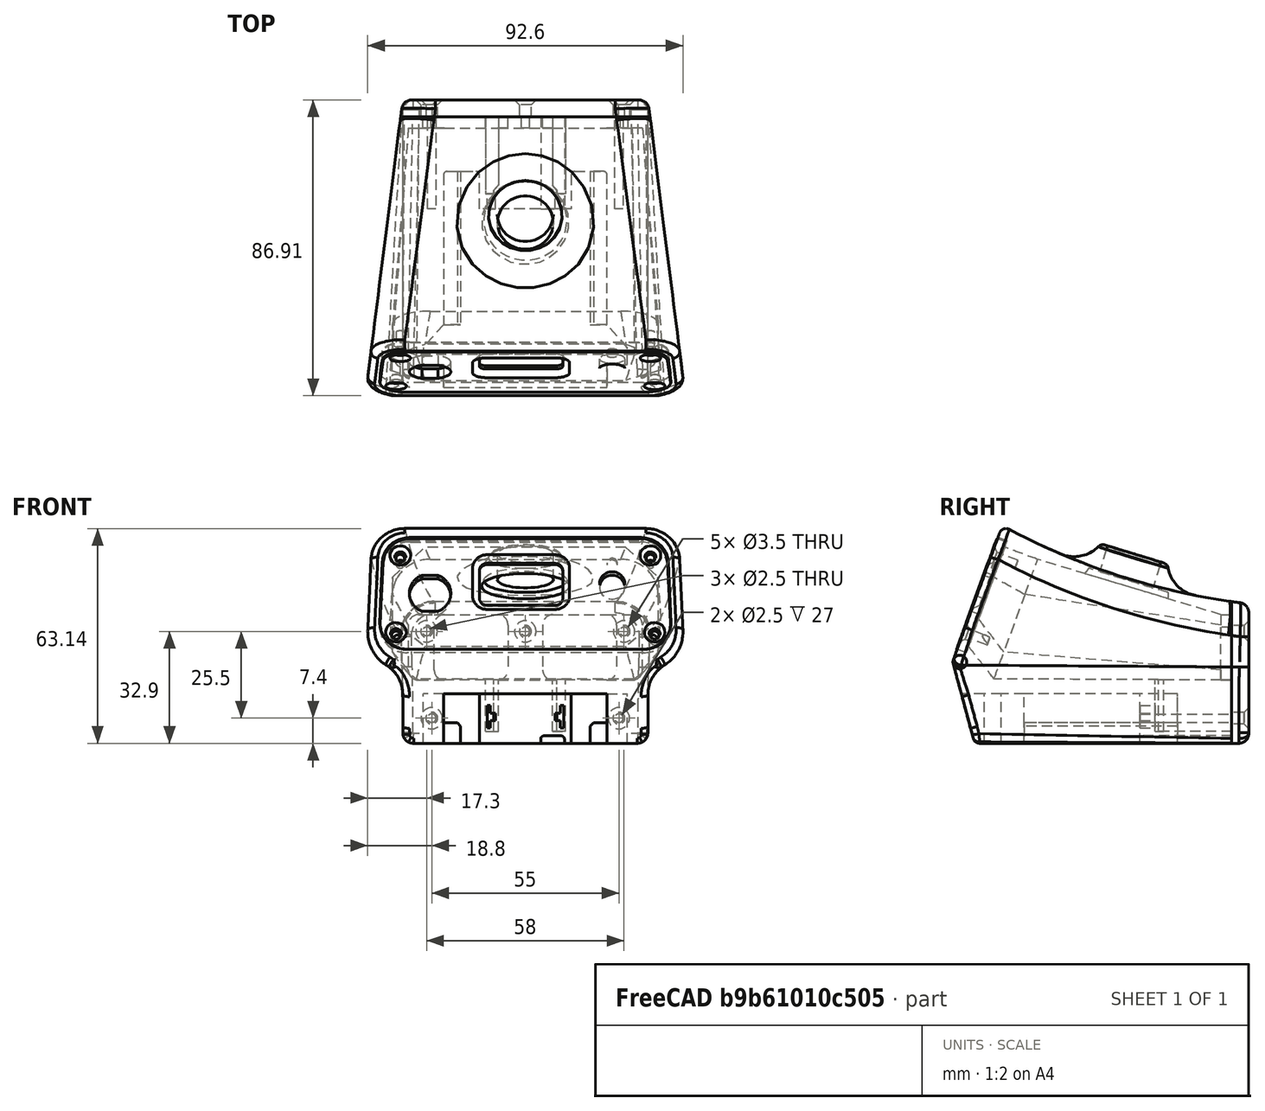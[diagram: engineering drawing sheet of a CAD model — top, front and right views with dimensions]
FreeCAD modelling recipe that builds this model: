
FCSTD DOCUMENT  (FreeCAD 2022.709R28846 (Git))
Label: solder_station4a_snap
License: All rights reserved
LicenseURL: http://en.wikipedia.org/wiki/All_rights_reserved
objects: Sketcher::SketchObject×20, PartDesign::Pocket×10, PartDesign::Fillet×7, Mesh::Feature×4, Part::FeaturePython×3, App::DocumentObjectGroup×3, PartDesign::Chamfer×3, PartDesign::Body×3, PartDesign::FeatureBase×2, PartDesign::Pad×2, Spreadsheet::Sheet×1, Part::Plane×1, Part::Loft×1, Part::Extrusion×1, Part::MultiCommon×1, PartDesign::SubtractiveLoft×1, PartDesign::Revolution×1, PartDesign::Groove×1, App::Part×1
note: 109 computed .brp shape members not serialized (recipe doc carries the construction recipe); baked Part::Feature solids carry a one-line shape summary decoded from their .brp

FEATURE [Sketcher::SketchObject] Sketch  label="RearSupport"
  ArcFitTolerance = 0
  AttachmentOffset = pos=(0,0,-37.8) rot=(0,0,1;0rad)
  AttachmentSupport = -> [XZ_Plane005]
  FullyConstrained = true
  MapMode = 5
  Placement = pos=(0,37.8,8.4e-15) rot=(1,0,0;1.5708rad)
  Support = -> [XZ_Plane005]
  TreeRank = 0
  expr: AttachmentOffset.Base.z = -<<param>>.mid_depth / 2 + <<param>>.wall
  expr: Constraints[24] = 3
  expr: Constraints[37] = <<param>>.bottom_height
  expr: Constraints[38] = <<param>>.floor
  expr: Constraints[39] = <<param>>.rear_height - <<param>>.wall
  expr: Constraints[47] = <<param>>.reart_screw_width2
  expr: Constraints[48] = <<param>>.rear_screw_width1
  expr: Constraints[49] = <<param>>.screw_hole
  expr: Constraints[50] = <<param>>.rear_screw_height
  expr: Constraints[51] = <<param>>.rear_screw_height
  expr: Constraints[52] = <<param>>.rear_screw_offset
  sketch-geometry (22):
    g0: LineSegment StartX=-23.8 StartY=13.8 StartZ=0 EndX=-8.1 EndY=13.8 EndZ=0
    g1: LineSegment StartX=26.8 StartY=10.8 StartZ=0 EndX=26.8 EndY=-2.4 EndZ=0
    g2: LineSegment StartX=23.8 StartY=-5.4 StartZ=0 EndX=8.1 EndY=-5.4 EndZ=0
    g3: LineSegment StartX=-26.8 StartY=-2.4 StartZ=0 EndX=-26.8 EndY=10.8 EndZ=0
    g4: LineSegment StartX=-5.1 StartY=10.8 StartZ=0 EndX=-5.1 EndY=-2.4 EndZ=0
    g5: LineSegment StartX=5.1 StartY=10.8 StartZ=0 EndX=5.1 EndY=-2.4 EndZ=0
    g6: LineSegment StartX=8.1 StartY=13.8 StartZ=0 EndX=23.8 EndY=13.8 EndZ=0
    g7: LineSegment StartX=-8.1 StartY=-5.4 StartZ=0 EndX=-23.8 EndY=-5.4 EndZ=0
    g8: ArcOfCircle CenterX=-8.1 CenterY=10.8 CenterZ=0 NormalX=0 NormalY=0 NormalZ=1 AngleXU=0 Radius=3 StartAngle=0 EndAngle=1.5708
    g9: ArcOfCircle CenterX=8.1 CenterY=10.8 CenterZ=0 NormalX=0 NormalY=0 NormalZ=1 AngleXU=0 Radius=3 StartAngle=1.5708 EndAngle=3.14159
    g10: ArcOfCircle CenterX=-8.1 CenterY=-2.4 CenterZ=0 NormalX=0 NormalY=0 NormalZ=1 AngleXU=0 Radius=3 StartAngle=4.71239 EndAngle=6.28319
    g11: ArcOfCircle CenterX=8.1 CenterY=-2.4 CenterZ=0 NormalX=0 NormalY=0 NormalZ=1 AngleXU=0 Radius=3 StartAngle=3.14159 EndAngle=4.71239
    g12: ArcOfCircle CenterX=-23.8 CenterY=10.8 CenterZ=0 NormalX=0 NormalY=0 NormalZ=1 AngleXU=0 Radius=3 StartAngle=1.5708 EndAngle=3.14159
    g13: ArcOfCircle CenterX=-23.8 CenterY=-2.4 CenterZ=0 NormalX=0 NormalY=0 NormalZ=1 AngleXU=0 Radius=3 StartAngle=3.14159 EndAngle=4.71239
    g14: ArcOfCircle CenterX=23.8 CenterY=10.8 CenterZ=0 NormalX=0 NormalY=0 NormalZ=1 AngleXU=0 Radius=3 StartAngle=0 EndAngle=1.5708
    g15: ArcOfCircle CenterX=23.8 CenterY=-2.4 CenterZ=0 NormalX=0 NormalY=0 NormalZ=1 AngleXU=0 Radius=3 StartAngle=4.71239 EndAngle=6.28319
    g16: Circle [constr] CenterX=0 CenterY=-24 CenterZ=0 NormalX=0 NormalY=0 NormalZ=1 AngleXU=0 Radius=3
    g17: Circle CenterX=0 CenterY=8.9 CenterZ=0 NormalX=0 NormalY=0 NormalZ=1 AngleXU=0 Radius=1.25
    g18: Circle CenterX=-29 CenterY=8.9 CenterZ=0 NormalX=0 NormalY=0 NormalZ=1 AngleXU=0 Radius=1.25
    g19: Circle [constr] CenterX=-27.5 CenterY=-16.6 CenterZ=0 NormalX=0 NormalY=0 NormalZ=1 AngleXU=0 Radius=1.25
    g20: Circle [constr] CenterX=27.5 CenterY=-16.6 CenterZ=0 NormalX=0 NormalY=0 NormalZ=1 AngleXU=0 Radius=1.25
    g21: Circle CenterX=29 CenterY=8.9 CenterZ=0 NormalX=0 NormalY=0 NormalZ=1 AngleXU=0 Radius=1.25
  constraints (53):
    c: Horizontal(g0)
    c: Horizontal(g2)
    c: Vertical(g1)
    c: Vertical(g3)
    c: Vertical(g4)
    c: Vertical(g5)
    c: Tangent(g0,g6)
    c: Tangent(g2,g7)
    c: Tangent(g0,g8) = 1.5708
    c: Tangent(g4,g8) = 1.5708
    c: Tangent(g5,g9) = -1.5708
    c: Tangent(g6,g9) = 1.5708
    c: Tangent(g7,g10) = 1.5708
    c: Tangent(g4,g10) = 1.5708
    c: Tangent(g5,g11) = -1.5708
    c: Tangent(g2,g11) = 1.5708
    c: Tangent(g0,g12) = 1.5708
    c: Tangent(g3,g12) = 1.5708
    c: Tangent(g3,g13) = 1.5708
    c: Tangent(g7,g13) = 1.5708
    c: Tangent(g6,g14) = 1.5708
    c: Tangent(g1,g14) = 1.5708
    c: Tangent(g1,g15) = 1.5708
    c: Tangent(g2,g15) = 1.5708
    c: Radius(g9) = 3
    c: Equal(g12,g13)
    c: Equal(g13,g10)
    c: Equal(g10,g8)
    c: Equal(g11,g15)
    c: Equal(g15,g14)
    c: Equal(g14,g9)
    c: DistanceX(g4,g-1) = 5.1
    c: DistanceX(g5,g1) = 21.7
    c: Symmetric(g4,g5,g-2)
    c: Equal(g7,g2)
    c: PointOnObject(g16,g-2)
    c: Radius(g16) = 3
    c: DistanceY(g16,g-1) = 24
    c: DistanceY(g16,g2) = 18.6
    c: DistanceY(g16,g6) = 37.8
    c: PointOnObject(g17,g-2)
    c: Equal(g21,g18)
    c: Equal(g18,g19)
    c: Equal(g19,g20)
    c: Equal(g18,g17)
    c: Symmetric(g20,g19,g-2)
    c: Symmetric(g18,g21,g-2)
    c: DistanceX(g19,g20) = 55
    c: DistanceX(g18,g21) = 58
    c: Diameter(g19) = 2.5
    c: DistanceY(g20,g21) = 25.5
    c: DistanceY(g20,g17) = 25.5
    c: DistanceY(g16,g19) = 7.4
FEATURE [Spreadsheet::Sheet] Spreadsheet  label="param"
  PythonMode = false
  ShowCells = 0
  TreeRank = 0
  cells = A1=Body; B2=top_depth; C2(top_depth)=70; B3=mid_depth; C3(mid_depth)=82; D3=Half value is the rear reference point; B4=bottom_depth; C4(bottom_depth)=75; B6=bottom_width; C6(bottom_width)=72; B7=bottom_height; C7(bottom_height)=24; B8=bottom_angle; C8(bottom_angle)=15; B10=rear_width; C10(rear_width)=72; B11=rear_height; C11(rear_height)=41; B13=mid_width; C13(mid_width)=80; B14=mid_height; C14(mid_height)=50; B16=front_width1; C16(front_width1)=91; D16=@top (upper); B17=front_width2; C17(front_width2)=94; D17=@mid (lower); B18=front_height; C18(front_height)=64; B19=front_angle; C19(front_angle)=20; D19=20 is actual value; B21=wall; C21(wall)=3.2; B22=radius_big; C22(radius_big)=10; B23=radius_small; C23(radius_small)=3; B24=arch; C24(arch)=200; A26=Button; B27=button_offset; C27(button_offset)=10; B28=button_inside_dia; C28(button_inside_dia)=20; B29=button_outside_dia; C29(button_outside_dia)=22; B30=button_height; C30(button_height)=24; B31=button_extension; C31(button_extension)=8; B32=button_fillet; C32(button_fillet)=12; B33=button_angle; C33(button_angle)=-17; B34=button_hole; C34(button_hole)=16.4; B35=button_hole_center; C35(button_hole_center)=-0.5; A37=Battery Cuts; B38=batt_carveout; C38(batt_carveout)=14.6; B39=batt_rail; C39(batt_rail)=6; B40=batt_rail_length; C40(batt_rail_length)=45; A42=Terminal Pockets; B43=terminal_height; C43(terminal_height)=6.6; B44=terminal_thickness; C44(terminal_thickness)=1; B45=terminal_seperation; C45(terminal_seperation)=21.5; B46=terminal_offset; C46(terminal_offset)=4.5; B47=terminal_depth; C47(terminal_depth)=22.5; A49=Box Interior; B50=floor; C50(floor)=18.6; B51=rear_inside_width; C51(rear_inside_width)==C10 - C21; D51=Calculated; B52=rear_inside_height; C52(rear_inside_height)==C11 - C21; D52=Calculated; B53=mid_inside_width; C53(mid_inside_width)==C13; D53=Calculated; B54=mid_inside_height; C54(mid_inside_height)==C14 + 6; D54=Calculated; B55=front_inside_width1; C55(front_inside_width1)==C62 - C58 * 2; D55=Calculated (upper); B56=front_inside_width2; C56(front_inside_width2)==C63 - C58 * 2; D56=Calculated (lower); B57=front_inside_height; C57(front_inside_height)==C64 - C59 * 2; D57=Calculated; B58=front_width_lip_width; C58(front_width_lip_width)=3; B59=front_inside_lip_height; C59(front_inside_lip_height)=2; A61=Face; B62=face_width1; C62(face_width1)=84; D62=Dimension of opening in case (upper); B63=face_width2; C63(face_width2)=85.5; D63=Dimension of opening in case (lower); B64=face_height; C64(face_height)==34 + 1; D64=Dimension of actual opening in case; B65=face_fit; C65(face_fit)=0.4; D65=Reduction of face dimensions for clearance with case; B66=face_thickness; C66(face_thickness)=3; D66=Face thickness; B67=face_radius; C67(face_radius)=8; D67=Corner radius; B68=face_offset; C68(face_offset)=2.8; D68=Axis origin to bottom face (reference); B69=face_knob_x; C69(face_knob_x)=25.5; D69=Vertical center line of face to center of knob; B70=face_knob_y; C70(face_knob_y)=20.5; D70=Bottom of face to center of knob; B71=face_knob_tab; C71(face_knob_tab)=7; D71=Center to center distance of rotary dial shaft to tab; B72=face_knob_hole; C72(face_knob_hole)=7.4; D72=Hole size fo shaft; B73=face_screen_x; C73(face_screen_x)=14.5; D73=Center of knob to right edge of screen; B74=face_screen_y; C74(face_screen_y)=21; D74=Bottom of face to center of screen; B75=face_screen_width; C75(face_screen_width)=24.5; D75=Width of screen opening; B76=face_screen_height; C76(face_screen_height)=13.1; D76=Height of screen opening; B77=face_screen_radius; C77(face_screen_radius)=2.25; D77=Radius of screen opening; B78=face_plug_x; C78(face_plug_x)=28; D78=Center line of face to center of plug; B79=face_plug_y; C79(face_plug_y)=17.5; D79=Bottom of face to center of plug; B80=face_plug_hole; C80(face_plug_hole)=12.2; D80=Hole size for plug body; A82=Screws; B83=screw_hole; C83(screw_hole)=2.5; D83=Screw hole diameter; B85=front_screw_width1; C85(front_screw_width1)=73.5; D85=Screw center to center distance (upper); B86=front_screw_width2; C86(front_screw_width2)=76; D86=Screw center to center distance (lower); B87=front_screw_height; C87(front_screw_height)=24; D87=Screw center to center distance (top to bottom); B88=front_screw_offset; C88(front_screw_offset)=5.5; D88=Bottom of face to center of screws (lower); B90=rear_screw_width1; C90(rear_screw_width1)=58; D90=Screw center to center distance (upper); B91=reart_screw_width2; C91(reart_screw_width2)=55; D91=Screw center to center distance (lower); B92=rear_screw_height; C92(rear_screw_height)=25.5; D92=Screw center to center distance (top to bottom); B93=rear_screw_offset; C93(rear_screw_offset)=7.4; A95=Back; B96=back_thickness; C96(back_thickness)=5
FEATURE [Sketcher::SketchObject] Sketch008  label="SketchButtonHole"
  ArcFitTolerance = 0
  AttachmentOffset = pos=(0,-0.5,24) rot=(1,0,0;-0.296706rad)
  AttachmentSupport = -> [XY_Plane005]
  FullyConstrained = true
  MapMode = 5
  Placement = pos=(0,-0.5,24) rot=(1,0,0;5.98648rad)
  Support = -> [XY_Plane005]
  TreeRank = 0
  expr: AttachmentOffset.Base.y = <<param>>.button_hole_center
  expr: AttachmentOffset.Base.z = <<param>>.button_height
  expr: AttachmentOffset.Rotation.Angle = <<param>>.button_angle
  expr: Constraints[0] = <<param>>.button_hole
  expr: Constraints[2] = <<param>>.button_offset
  sketch-geometry (1):
    g0: Circle CenterX=0 CenterY=10 CenterZ=0 NormalX=0 NormalY=0 NormalZ=1 AngleXU=0 Radius=8.2
  constraints (3):
    c: Diameter(g0) = 16.4
    c: PointOnObject(g0,g-2)
    c: DistanceY(g-1,g0) = 10
FEATURE [Sketcher::SketchObject] Sketch012  label="SketchSide"
  ArcFitTolerance = 0
  AttachmentOffset = pos=(2.5,0,0) rot=(0,0,1;0rad)
  AttachmentSupport = -> [YZ_Plane006]
  FullyConstrained = true
  MapMode = 5
  Placement = pos=(6e-16,2.5,-6e-16) rot=(0.57735,0.57735,0.57735;2.0944rad)
  Support = -> [YZ_Plane006]
  TreeRank = 0
  expr: AttachmentOffset.Base.x = <<param>>.back_thickness / 2
  expr: Constraints[10] = <<param>>.bottom_height
  expr: Constraints[11] = 90 - <<param>>.bottom_angle
  expr: Constraints[12] = 90 - <<param>>.front_angle
  expr: Constraints[16] = <<param>>.front_height
  expr: Constraints[4] = <<param>>.rear_height - <<param>>.bottom_height
  expr: Constraints[5] = <<param>>.arch
  expr: Constraints[6] = <<param>>.mid_depth + <<param>>.back_thickness
  sketch-geometry (6):
    g0: LineSegment StartX=43.5 StartY=0 StartZ=0 EndX=43.5 EndY=17 EndZ=0
    g1: LineSegment StartX=-43.5 StartY=0 StartZ=0 EndX=-28.9412 EndY=40 EndZ=0
    g2: ArcOfCircle CenterX=66.6993 CenterY=215.65 CenterZ=0 NormalX=0 NormalY=0 NormalZ=1 AngleXU=0 Radius=200 StartAngle=4.21378 EndAngle=4.59613
    g3: LineSegment StartX=-43.5 StartY=0 StartZ=0 EndX=-37.0692 EndY=-24 EndZ=0
    g4: LineSegment StartX=-37.0692 StartY=-24 StartZ=0 EndX=43.5 EndY=-24 EndZ=0
    g5: LineSegment StartX=43.5 StartY=-24 StartZ=0 EndX=43.5 EndY=0 EndZ=0
  constraints (18):
    c: PointOnObject(g1,g-1)
    c: Vertical(g0)
    c: Coincident(g2,g0)
    c: Symmetric(g1,g0,g-2)
    c: DistanceY(g0,g0) = 17
    c: Radius(g2) = 200
    c: DistanceX(g1,g0) = 87
    c: Horizontal(g4)
    c: Coincident(g5,g4)
    c: Vertical(g5)
    c: DistanceY(g4,g-1) = 24
    c: Angle(g3,g-1) = 1.309
    c: Angle(g-1,g1) = 1.22173
    c: Coincident(g3,g1)
    c: Coincident(g5,g0)
    c: Coincident(g2,g1)
    c: DistanceY(g4,g1) = 64
    c: Coincident(g4,g3)
FEATURE [Sketcher::SketchObject] Sketch018  label="SketchBat1"
  ArcFitTolerance = 0
  AttachmentOffset = pos=(0,0,-24) rot=(0,0,1;0rad)
  AttachmentSupport = -> [XY_Plane005]
  FullyConstrained = true
  MapMode = 5
  Placement = pos=(0,0,-24) rot=(0,0,1;0rad)
  Support = -> [XY_Plane005]
  TreeRank = 0
  expr: AttachmentOffset.Base.z = -<<param>>.bottom_height
  expr: Constraints[63] = <<param>>.batt_rail_length
  expr: Constraints[64] = <<param>>.mid_depth / 2
  sketch-geometry (21):
    g0: LineSegment StartX=-24 StartY=-41.7082 StartZ=0 EndX=24 EndY=-41.7082 EndZ=0
    g1: LineSegment StartX=24 StartY=-41.7082 StartZ=0 EndX=24 EndY=-31.7082 EndZ=0
    g2: LineSegment StartX=24 StartY=-31.7082 StartZ=0 EndX=30 EndY=-31.7082 EndZ=0
    g3: LineSegment StartX=30 StartY=-31.7082 StartZ=0 EndX=30 EndY=-26.7082 EndZ=0
    g4: LineSegment StartX=30 StartY=-26.7082 StartZ=0 EndX=24 EndY=-20 EndZ=0
    g5: LineSegment StartX=24 StartY=-20 StartZ=0 EndX=24 EndY=24 EndZ=0
    g6: LineSegment StartX=13.5 StartY=24 StartZ=0 EndX=13.5 EndY=14 EndZ=0
    g7: LineSegment StartX=13.5 StartY=14 StartZ=0 EndX=-13.5 EndY=14 EndZ=0
    g8: LineSegment StartX=-13.5 StartY=14 StartZ=0 EndX=-13.5 EndY=24 EndZ=0
    g9: LineSegment StartX=-24 StartY=24 StartZ=0 EndX=-24 EndY=-20 EndZ=0
    g10: LineSegment StartX=-24 StartY=-20 StartZ=0 EndX=-30 EndY=-26.7082 EndZ=0
    g11: LineSegment StartX=-30 StartY=-26.7082 StartZ=0 EndX=-30 EndY=-31.7082 EndZ=0
    g12: LineSegment StartX=-30 StartY=-31.7082 StartZ=0 EndX=-24 EndY=-31.7082 EndZ=0
    g13: LineSegment StartX=-24 StartY=-31.7082 StartZ=0 EndX=-24 EndY=-41.7082 EndZ=0
    g14: Circle [constr] CenterX=0 CenterY=41 CenterZ=0 NormalX=0 NormalY=0 NormalZ=1 AngleXU=0 Radius=4
    g15: ArcOfCircle CenterX=-14.5 CenterY=24 CenterZ=0 NormalX=0 NormalY=0 NormalZ=1 AngleXU=0 Radius=1 StartAngle=6.28318 EndAngle=7.85399
    g16: LineSegment StartX=-23 StartY=25 StartZ=0 EndX=-14.5 EndY=25 EndZ=0
    g17: LineSegment StartX=14.5 StartY=25 StartZ=0 EndX=23 EndY=25 EndZ=0
    g18: ArcOfCircle CenterX=-23 CenterY=24 CenterZ=0 NormalX=0 NormalY=0 NormalZ=1 AngleXU=0 Radius=1 StartAngle=1.57079 EndAngle=3.1416
    g19: ArcOfCircle CenterX=14.5 CenterY=24 CenterZ=0 NormalX=0 NormalY=0 NormalZ=1 AngleXU=0 Radius=1 StartAngle=1.5708 EndAngle=3.14159
    g20: ArcOfCircle CenterX=23 CenterY=24 CenterZ=0 NormalX=0 NormalY=0 NormalZ=1 AngleXU=0 Radius=1.00001 StartAngle=2.75124e-06 EndAngle=1.5708
  constraints (65):
    c: Horizontal(g0)
    c: Coincident(g1,g0)
    c: Vertical(g1)
    c: Coincident(g2,g1)
    c: Horizontal(g2)
    c: Coincident(g3,g2)
    c: Coincident(g3,g4)
    c: Vertical(g5)
    c: Coincident(g6,g7)
    c: Coincident(g7,g8)
    c: Vertical(g8)
    c: Vertical(g9)
    c: Coincident(g10,g11)
    c: Vertical(g11)
    c: Coincident(g11,g12)
    c: Horizontal(g12)
    c: Coincident(g12,g13)
    c: Equal(g6,g8)
    c: Equal(g5,g9)
    c: Equal(g4,g10)
    c: Equal(g3,g11)
    c: Equal(g12,g2)
    c: Equal(g1,g13)
    c: Coincident(g13,g0)
    c: Vertical(g13)
    c: DistanceX(g7,g7) = 27
    c: Symmetric(g7,g6,g-2)
    c: Distance(g4) = 9
    c: Vertical(g3)
    c: DistanceY(g3,g3) = 5
    c: DistanceX(g2,g2) = 6
    c: DistanceY(g1,g1) = 10
    c: DistanceX(g0,g0) = 48
    c: PointOnObject(g14,g-2)
    c: Coincident(g9,g10)
    c: Coincident(g5,g4)
    c: Coincident(g15,g8)
    c: Coincident(g16,g15)
    c: Tangent(g15,g8)
    c: Horizontal(g16)
    c: Horizontal(g17)
    c: DistanceX(g9,g5) = 48
    c: Symmetric(g4,g9,g-2)
    c: Equal(g16,g17)
    c: Coincident(g18,g9)
    c: Coincident(g18,g16)
    c: Equal(g18,g15)
    c: Tangent(g18,g16)
    c: Tangent(g18,g9)
    c: DistanceY(g6,g17) = 11
    c: Vertical(g6)
    c: Coincident(g19,g6)
    c: Coincident(g19,g17)
    c: Coincident(g20,g17)
    c: Coincident(g20,g5)
    c: Tangent(g20,g17)
    c: Tangent(g20,g5)
    c: Tangent(g19,g6)
    c: Tangent(g19,g17)
    c: Equal(g15,g19)
    c: Radius(g19) = 1
    c: Radius(g14) = 4
    c: DistanceY(g15,g14) = 16
    c: DistanceY(g9,g16) = 45
    c: DistanceY(g-1,g14) = 41
FEATURE [Sketcher::SketchObject] Sketch019  label="SketchBat2"
  ArcFitTolerance = 0
  AttachmentOffset = pos=(0,0,-25) rot=(0,0,1;0rad)
  AttachmentSupport = -> [XZ_Plane005]
  FullyConstrained = true
  MapMode = 5
  Placement = pos=(0,25,5.6e-15) rot=(1,0,0;1.5708rad)
  Support = -> [XZ_Plane005]
  TreeRank = 0
  expr: AttachmentOffset.Base.z = -<<param>>.mid_depth / 2 + 16
  expr: Constraints[17] = <<param>>.bottom_height
  expr: Constraints[18] = <<param>>.batt_rail
  expr: Constraints[19] = 48.01mm
  sketch-geometry (10):
    g0: LineSegment StartX=-24.005 StartY=-18 StartZ=0 EndX=-20.005 EndY=-18 EndZ=0
    g1: LineSegment StartX=-19.005 StartY=-24 StartZ=0 EndX=-24.005 EndY=-24 EndZ=0
    g2: LineSegment StartX=-24.005 StartY=-24 StartZ=0 EndX=-24.005 EndY=-18 EndZ=0
    g3: LineSegment StartX=24.005 StartY=-18 StartZ=0 EndX=20.005 EndY=-18 EndZ=0
    g4: LineSegment StartX=19.005 StartY=-24 StartZ=0 EndX=24.005 EndY=-24 EndZ=0
    g5: LineSegment StartX=24.005 StartY=-24 StartZ=0 EndX=24.005 EndY=-18 EndZ=0
    g6: LineSegment StartX=-19.005 StartY=-19 StartZ=0 EndX=-19.005 EndY=-24 EndZ=0
    g7: LineSegment StartX=19.005 StartY=-24 StartZ=0 EndX=19.005 EndY=-19 EndZ=0
    g8: LineSegment StartX=-20.005 StartY=-18 StartZ=0 EndX=-19.005 EndY=-19 EndZ=0
    g9: LineSegment StartX=19.005 StartY=-19 StartZ=0 EndX=20.005 EndY=-18 EndZ=0
  constraints (29):
    c: Coincident(g1,g2)
    c: Coincident(g2,g0)
    c: Horizontal(g0)
    c: Horizontal(g1)
    c: Vertical(g2)
    c: Coincident(g4,g5)
    c: Coincident(g5,g3)
    c: Horizontal(g3)
    c: Horizontal(g4)
    c: Vertical(g5)
    c: Coincident(g6,g1)
    c: Vertical(g6)
    c: Equal(g1,g4)
    c: Coincident(g7,g4)
    c: Vertical(g7)
    c: Equal(g6,g7)
    c: Symmetric(g1,g4,g-2)
    c: DistanceY(g1,g-1) = 24
    c: DistanceY(g4,g3) = 6
    c: DistanceX(g1,g4) = 48.01
    c: DistanceX(g4,g4) = 5
    c: Coincident(g8,g0)
    c: Coincident(g8,g6)
    c: Coincident(g9,g7)
    c: Coincident(g9,g3)
    c: Equal(g0,g3)
    c: Equal(g2,g5)
    c: DistanceX(g0,g0) = 4
    c: DistanceY(g1,g6) = 5
FEATURE [Sketcher::SketchObject] Sketch021  label="SketchButton"
  ArcFitTolerance = 0
  AttachmentOffset = pos=(10,24,0) rot=(0,0,1;-0.296706rad)
  AttachmentSupport = -> [YZ_Plane005]
  FullyConstrained = true
  MapMode = 5
  Placement = pos=(-3.1e-15,10,24) rot=(-0.51122,-0.690875,-0.51122;4.35074rad)
  Support = -> [YZ_Plane005]
  TreeRank = 0
  expr: AttachmentOffset.Base.x = <<param>>.button_offset
  expr: AttachmentOffset.Base.y = <<param>>.button_height
  expr: AttachmentOffset.Rotation.Angle = <<param>>.button_angle
  expr: Constraints[6] = <<param>>.button_extension
  expr: Constraints[7] = <<param>>.button_outside_dia / 2
  sketch-geometry (5):
    g0: LineSegment StartX=0 StartY=0 StartZ=0 EndX=0 EndY=8 EndZ=0
    g1: LineSegment StartX=0 StartY=8 StartZ=0 EndX=9 EndY=8 EndZ=0
    g2: LineSegment StartX=0 StartY=0 StartZ=0 EndX=11 EndY=0 EndZ=0
    g3: LineSegment StartX=11 StartY=0 StartZ=0 EndX=11 EndY=6 EndZ=0
    g4: ArcOfCircle CenterX=9 CenterY=6 CenterZ=0 NormalX=0 NormalY=0 NormalZ=1 AngleXU=0 Radius=2 StartAngle=1.123e-13 EndAngle=1.5708
  constraints (13):
    c: Coincident(g0,g-1)
    c: PointOnObject(g0,g-2)
    c: Coincident(g1,g0)
    c: Horizontal(g1)
    c: Coincident(g2,g0)
    c: Horizontal(g2)
    c: DistanceY(g0,g0) = 8
    c: DistanceX(g2,g2) = 11
    c: Coincident(g3,g2)
    c: Vertical(g3)
    c: Radius(g4) = 2
    c: Tangent(g4,g3) = -1.5708
    c: Tangent(g4,g1) = 1.5708
FEATURE [Sketcher::SketchObject] Sketch022  label="SketchRearInside"
  ArcFitTolerance = 0
  AttachmentOffset = pos=(0,0,-37.8) rot=(0,0,1;0rad)
  AttachmentSupport = -> [XZ_Plane005]
  FullyConstrained = true
  MapMode = 5
  Placement = pos=(0,37.8,8.4e-15) rot=(1,0,0;1.5708rad)
  Support = -> [XZ_Plane005]
  TreeRank = 0
  expr: AttachmentOffset.Base.z = -<<param>>.mid_depth / 2 + <<param>>.wall
  expr: Constraints[12] = <<param>>.radius_small
  expr: Constraints[18] = <<param>>.rear_inside_width
  expr: Constraints[26] = <<param>>.bottom_height
  expr: Constraints[27] = <<param>>.rear_inside_height
  expr: Constraints[29] = <<param>>.floor
  sketch-geometry (9):
    g0: LineSegment StartX=-34.4 StartY=10.8 StartZ=0 EndX=-34.4 EndY=-2.39998 EndZ=0
    g1: LineSegment StartX=-31.4 StartY=-5.4 StartZ=0 EndX=31.4 EndY=-5.4 EndZ=0
    g2: LineSegment StartX=34.4 StartY=-2.39998 StartZ=0 EndX=34.4 EndY=10.8 EndZ=0
    g3: LineSegment StartX=-31.4 StartY=13.8 StartZ=0 EndX=31.4 EndY=13.8 EndZ=0
    g4: ArcOfCircle CenterX=31.4 CenterY=10.8 CenterZ=0 NormalX=0 NormalY=0 NormalZ=1 AngleXU=0 Radius=3 StartAngle=6.28318 EndAngle=7.85399
    g5: ArcOfCircle CenterX=31.4 CenterY=-2.4 CenterZ=0 NormalX=0 NormalY=0 NormalZ=1 AngleXU=0 Radius=3 StartAngle=4.71238 EndAngle=6.28319
    g6: ArcOfCircle CenterX=-31.4 CenterY=10.8 CenterZ=0 NormalX=0 NormalY=0 NormalZ=1 AngleXU=0 Radius=3 StartAngle=1.57079 EndAngle=3.1416
    g7: ArcOfCircle CenterX=-31.4 CenterY=-2.4 CenterZ=0 NormalX=0 NormalY=0 NormalZ=1 AngleXU=0 Radius=3 StartAngle=3.14159 EndAngle=4.71239
    g8: Circle [constr] CenterX=0 CenterY=-24 CenterZ=0 NormalX=0 NormalY=0 NormalZ=1 AngleXU=0 Radius=3
  constraints (30):
    c: Vertical(g0)
    c: Horizontal(g1)
    c: Vertical(g2)
    c: Horizontal(g3)
    c: Equal(g3,g1)
    c: Equal(g0,g2)
    c: Coincident(g4,g3)
    c: Coincident(g4,g2)
    c: Coincident(g5,g2)
    c: Coincident(g5,g1)
    c: Coincident(g6,g0)
    c: Coincident(g6,g3)
    c: Radius(g6) = 3
    c: Equal(g6,g4)
    c: Equal(g4,g5)
    c: Coincident(g7,g1)
    c: Coincident(g7,g0)
    c: Equal(g5,g7)
    c: DistanceX(g0,g2) = 68.8
    c: Symmetric(g0,g2,g-2)
    c: Tangent(g4,g2)
    c: Tangent(g4,g3)
    c: Tangent(g5,g2)
    c: Tangent(g5,g1)
    c: Tangent(g6,g3)
    c: PointOnObject(g8,g-2)
    c: DistanceY(g8,g-1) = 24
    c: DistanceY(g8,g3) = 37.8
    c: Radius(g8) = 3
    c: DistanceY(g8,g1) = 18.6
FEATURE [Sketcher::SketchObject] Sketch023  label="SketchFrontInside"
  ArcFitTolerance = 0
  AttachmentOffset = pos=(0,0,38) rot=(1,0,0;-0.349066rad)
  AttachmentSupport = -> [XZ_Plane005]
  FullyConstrained = true
  MapMode = 5
  Placement = pos=(0,-38,-8.4e-15) rot=(-1,0,0;5.06145rad)
  Support = -> [XZ_Plane005]
  TreeRank = 0
  expr: AttachmentOffset.Base.z = <<param>>.mid_depth / 2 - <<param>>.face_thickness
  expr: AttachmentOffset.Rotation.Angle = -<<param>>.front_angle
  expr: Constraints[19] = <<param>>.front_inside_width2
  expr: Constraints[1] = <<param>>.front_inside_width1
  expr: Constraints[20] = <<param>>.front_inside_width2 / 2
  expr: Constraints[21] = <<param>>.face_offset + <<param>>.front_inside_lip_height
  expr: Constraints[2] = <<param>>.front_inside_height
  sketch-geometry (8):
    g0: LineSegment StartX=-29.5 StartY=4.8 StartZ=0 EndX=29.5 EndY=4.8 EndZ=0
    g1: LineSegment StartX=29.5 StartY=35.8 StartZ=0 EndX=-29.5 EndY=35.8 EndZ=0
    g2: LineSegment StartX=-39 StartY=26.3885 StartZ=0 EndX=-39.75 EndY=13.3885 EndZ=0
    g3: LineSegment StartX=-39 StartY=26.3885 StartZ=0 EndX=-29.5 EndY=35.8 EndZ=0
    g4: LineSegment StartX=29.5 StartY=35.8 StartZ=0 EndX=39 EndY=26.3885 EndZ=0
    g5: LineSegment StartX=39.75 StartY=13.3885 StartZ=0 EndX=29.5 EndY=4.8 EndZ=0
    g6: LineSegment StartX=-39.75 StartY=13.3885 StartZ=0 EndX=-29.5 EndY=4.8 EndZ=0
    g7: LineSegment StartX=39 StartY=26.3885 StartZ=0 EndX=39.75 EndY=13.3885 EndZ=0
  constraints (22):
    c: Symmetric(g0,g0,g-2)
    c: DistanceX(g2,g4) = 78
    c: DistanceY(g0,g1) = 31
    c: Symmetric(g1,g1,g-2)
    c: Coincident(g3,g2)
    c: Coincident(g3,g1)
    c: Coincident(g4,g1)
    c: Coincident(g5,g0)
    c: Coincident(g6,g2)
    c: Coincident(g6,g0)
    c: Equal(g3,g6)
    c: Equal(g6,g5)
    c: Equal(g5,g4)
    c: Coincident(g7,g4)
    c: Coincident(g7,g5)
    c: DistanceY(g7,g7) = 13
    c: Equal(g7,g2)
    c: Equal(g1,g0)
    c: DistanceX(g1,g1) = 59
    c: DistanceX(g2,g5) = 79.5
    c: DistanceX(g2,g-1) = 39.75
    c: DistanceY(g-1,g0) = 4.8
FEATURE [Sketcher::SketchObject] Sketch024  label="SketchFaceCut"
  ArcFitTolerance = 0
  AttachmentOffset = pos=(0,0,38) rot=(1,0,0;-0.349066rad)
  AttachmentSupport = -> [XZ_Plane005]
  FullyConstrained = true
  MapMode = 5
  Placement = pos=(0,-38,-8.4e-15) rot=(-1,0,0;5.06145rad)
  Support = -> [XZ_Plane005]
  TreeRank = 0
  expr: AttachmentOffset.Base.z = <<param>>.mid_depth / 2 - <<param>>.face_thickness
  expr: AttachmentOffset.Rotation.Angle = -<<param>>.front_angle
  expr: Constraints[13] = <<param>>.face_radius
  expr: Constraints[22] = <<param>>.face_width1
  expr: Constraints[23] = <<param>>.face_width2
  expr: Constraints[24] = <<param>>.face_offset
  expr: Constraints[25] = <<param>>.face_height
  sketch-geometry (8):
    g0: LineSegment StartX=-34.0063 StartY=37.8 StartZ=0 EndX=34.0063 EndY=37.8 EndZ=0
    g1: LineSegment StartX=42 StartY=30.1155 StartZ=0 EndX=42.75 EndY=11.1155 EndZ=0
    g2: LineSegment StartX=34.7563 StartY=2.8 StartZ=0 EndX=-34.7563 EndY=2.8 EndZ=0
    g3: LineSegment StartX=-42.75 StartY=11.1155 StartZ=0 EndX=-42 EndY=30.1155 EndZ=0
    g4: ArcOfCircle CenterX=34.0062 CenterY=29.8 CenterZ=0 NormalX=0 NormalY=0 NormalZ=1 AngleXU=0 Radius=8 StartAngle=0.0394512 EndAngle=1.57079
    g5: ArcOfCircle CenterX=34.7562 CenterY=10.8 CenterZ=0 NormalX=0 NormalY=0 NormalZ=1 AngleXU=0 Radius=8 StartAngle=4.71239 EndAngle=6.32264
    g6: ArcOfCircle CenterX=-34.0062 CenterY=29.8 CenterZ=0 NormalX=0 NormalY=0 NormalZ=1 AngleXU=0 Radius=8 StartAngle=1.5708 EndAngle=3.10214
    g7: ArcOfCircle CenterX=-34.7562 CenterY=10.8 CenterZ=0 NormalX=0 NormalY=0 NormalZ=1 AngleXU=0 Radius=8 StartAngle=3.10214 EndAngle=4.71239
  constraints (27):
    c: Horizontal(g0)
    c: Coincident(g4,g0)
    c: Coincident(g4,g1)
    c: Coincident(g5,g1)
    c: Coincident(g5,g2)
    c: Coincident(g6,g0)
    c: Coincident(g6,g3)
    c: Coincident(g7,g3)
    c: Coincident(g7,g2)
    c: Equal(g1,g3)
    c: Equal(g4,g6)
    c: Equal(g6,g7)
    c: Equal(g7,g5)
    c: Radius(g4) = 8
    c: Tangent(g6,g3)
    c: Tangent(g7,g3)
    c: Tangent(g7,g2)
    c: Tangent(g6,g0)
    c: Tangent(g4,g0)
    c: Tangent(g4,g1)
    c: Tangent(g5,g1)
    c: Tangent(g5,g2)
    c: DistanceX(g3,g1) = 84
    c: DistanceX(g3,g1) = 85.5
    c: DistanceY(g-1,g2) = 2.8
    c: DistanceY(g2,g0) = 35
    c: Symmetric(g2,g2,g-2)
FEATURE [Sketcher::SketchObject] Sketch025  label="SketchMidInside"
  ArcFitTolerance = 0
  AttachmentOffset = pos=(0,0,27) rot=(1,0,0;-0.349066rad)
  AttachmentSupport = -> [XZ_Plane005]
  FullyConstrained = true
  MapMode = 5
  Placement = pos=(0,-27,-6e-15) rot=(-1,0,0;5.06145rad)
  Support = -> [XZ_Plane005]
  TreeRank = 0
  expr: AttachmentOffset.Base.z = <<param>>.mid_depth / 2 - 14
  expr: AttachmentOffset.Rotation.Angle = -<<param>>.front_angle
  expr: Constraints[10] = <<param>>.radius_big + 1
  expr: Constraints[11] = <<param>>.floor
  expr: Constraints[12] = Spreadsheet.mid_inside_width - 2
  expr: Constraints[14] = <<param>>.mid_inside_height
  expr: Constraints[23] = <<param>>.mid_width - 16
  expr: Constraints[4] = <<param>>.bottom_height
  sketch-geometry (9):
    g0: LineSegment StartX=-28 StartY=32 StartZ=0 EndX=28 EndY=32 EndZ=0
    g1: LineSegment StartX=39 StartY=21 StartZ=0 EndX=39 EndY=3 EndZ=0
    g2: LineSegment StartX=32 StartY=-5.4 StartZ=0 EndX=-32 EndY=-5.4 EndZ=0
    g3: LineSegment StartX=-39 StartY=3 StartZ=0 EndX=-39 EndY=21 EndZ=0
    g4: Circle [constr] CenterX=0 CenterY=-24 CenterZ=0 NormalX=0 NormalY=0 NormalZ=1 AngleXU=0 Radius=3
    g5: ArcOfCircle CenterX=-28 CenterY=21 CenterZ=0 NormalX=0 NormalY=0 NormalZ=1 AngleXU=0 Radius=11 StartAngle=1.5708 EndAngle=3.14159
    g6: ArcOfCircle CenterX=28 CenterY=21 CenterZ=0 NormalX=0 NormalY=0 NormalZ=1 AngleXU=0 Radius=11 StartAngle=0 EndAngle=1.5708
    g7: ArcOfCircle CenterX=-17.5474 CenterY=13.7605 CenterZ=0 NormalX=0 NormalY=0 NormalZ=1 AngleXU=0 Radius=24 StartAngle=3.60651 EndAngle=4.06615
    g8: ArcOfCircle CenterX=17.5474 CenterY=13.7605 CenterZ=0 NormalX=0 NormalY=0 NormalZ=1 AngleXU=0 Radius=24 StartAngle=5.35863 EndAngle=5.81826
  constraints (25):
    c: Vertical(g1)
    c: Vertical(g3)
    c: PointOnObject(g4,g-2)
    c: Radius(g4) = 3
    c: DistanceY(g4,g-1) = 24
    c: Tangent(g3,g5) = 1.5708
    c: Tangent(g0,g5) = 1.5708
    c: Tangent(g0,g6) = 1.5708
    c: Tangent(g1,g6) = 1.5708
    c: Equal(g6,g5)
    c: Radius(g6) = 11
    c: DistanceY(g4,g2) = 18.6
    c: DistanceX(g3,g1) = 78
    c: Symmetric(g2,g2,g-2)
    c: DistanceY(g4,g0) = 56
    c: Symmetric(g0,g0,g-2)
    c: Equal(g3,g1)
    c: Coincident(g7,g2)
    c: Coincident(g8,g1)
    c: Coincident(g8,g2)
    c: Coincident(g7,g3)
    c: Equal(g8,g7)
    c: Radius(g8) = 24
    c: DistanceX(g2,g2) = 64
    c: DistanceY(g1,g1) = 18
FEATURE [Sketcher::SketchObject] Sketch026  label="SketchFrontScrews"
  ArcFitTolerance = 0
  AttachmentOffset = pos=(0,0,38) rot=(1,0,0;-0.349066rad)
  AttachmentSupport = -> [XZ_Plane005]
  FullyConstrained = true
  MapMode = 5
  Placement = pos=(0,-38,-8.4e-15) rot=(-1,0,0;5.06145rad)
  Support = -> [XZ_Plane005]
  TreeRank = 0
  expr: AttachmentOffset.Base.z = <<param>>.mid_depth / 2 - <<param>>.face_thickness
  expr: AttachmentOffset.Rotation.Angle = -<<param>>.front_angle
  expr: Constraints[0] = <<param>>.front_screw_width1
  expr: Constraints[13] = <<param>>.screw_hole
  expr: Constraints[1] = <<param>>.front_screw_width2
  expr: Constraints[2] = <<param>>.front_screw_height
  expr: Constraints[9] = <<param>>.face_offset + <<param>>.front_screw_offset
  sketch-geometry (6):
    g0: Circle CenterX=-36.75 CenterY=32.3 CenterZ=0 NormalX=0 NormalY=0 NormalZ=1 AngleXU=0 Radius=1.25
    g1: Circle CenterX=36.75 CenterY=32.3 CenterZ=0 NormalX=0 NormalY=0 NormalZ=1 AngleXU=0 Radius=1.25
    g2: Circle CenterX=-38 CenterY=8.3 CenterZ=0 NormalX=0 NormalY=0 NormalZ=1 AngleXU=0 Radius=1.25
    g3: Circle CenterX=38 CenterY=8.3 CenterZ=0 NormalX=0 NormalY=0 NormalZ=1 AngleXU=0 Radius=1.25
    g4: LineSegment [constr] StartX=-36.75 StartY=32.3 StartZ=0 EndX=36.75 EndY=32.3 EndZ=0
    g5: LineSegment [constr] StartX=-38 StartY=8.3 StartZ=0 EndX=38 EndY=8.3 EndZ=0
  constraints (14):
    c: DistanceX(g0,g1) = 73.5
    c: DistanceX(g2,g3) = 76
    c: DistanceY(g3,g1) = 24
    c: Coincident(g4,g0)
    c: Coincident(g4,g1)
    c: Coincident(g5,g2)
    c: Coincident(g5,g3)
    c: Symmetric(g2,g3,g-2)
    c: Symmetric(g0,g1,g-2)
    c: DistanceY(g-1,g3) = 8.3
    c: Equal(g0,g2)
    c: Equal(g2,g3)
    c: Equal(g3,g1)
    c: Diameter(g0) = 2.5
FEATURE [Sketcher::SketchObject] Sketch027  label="SketchButtonCarve"
  ArcFitTolerance = 0
  AttachmentOffset = pos=(10,22,0) rot=(0,0,1;-0.296706rad)
  AttachmentSupport = -> [YZ_Plane005]
  FullyConstrained = true
  MapMode = 5
  Placement = pos=(-2.7e-15,10,22) rot=(-0.51122,-0.690875,-0.51122;4.35074rad)
  Support = -> [YZ_Plane005]
  TreeRank = 0
  expr: AttachmentOffset.Base.x = <<param>>.button_offset
  expr: AttachmentOffset.Base.y = <<param>>.button_height - 2
  expr: AttachmentOffset.Rotation.Angle = <<param>>.button_angle
  expr: Constraints[12] = <<param>>.button_hole / 2 + 10
  expr: Constraints[6] = <<param>>.button_hole / 2 + 4
  sketch-geometry (4):
    g0: LineSegment StartX=0 StartY=2 StartZ=0 EndX=12.2 EndY=2 EndZ=0
    g1: ArcOfCircle CenterX=18.2 CenterY=3.09999 CenterZ=0 NormalX=0 NormalY=0 NormalZ=1 AngleXU=0 Radius=6.09999 StartAngle=3.32291 EndAngle=4.71239
    g2: LineSegment StartX=0 StartY=2 StartZ=0 EndX=0 EndY=-3 EndZ=0
    g3: LineSegment StartX=18.2 StartY=-3 StartZ=0 EndX=0 EndY=-3 EndZ=0
  constraints (13):
    c: Horizontal(g0)
    c: Coincident(g1,g0)
    c: Coincident(g2,g0)
    c: Coincident(g3,g1)
    c: Horizontal(g3)
    c: Tangent(g3,g1)
    c: DistanceX(g0,g0) = 12.2
    c: DistanceY(g2,g2) = 5
    c: Coincident(g2,g3)
    c: Vertical(g2)
    c: PointOnObject(g-1,g2)
    c: DistanceY(g2,g-1) = 3
    c: DistanceX(g3,g3) = 18.2
FEATURE [Sketcher::SketchObject] Sketch028  label="SketchTerminals"
  ArcFitTolerance = 0
  AttachmentSupport = -> [XZ_Plane005]
  FullyConstrained = true
  MapMode = 5
  Placement = pos=(0,0,0) rot=(1,0,0;1.5708rad)
  Support = -> [XZ_Plane005]
  TreeRank = 0
  expr: Constraints[17] = <<param>>.terminal_thickness
  expr: Constraints[18] = <<param>>.terminal_height
  expr: Constraints[21] = <<param>>.bottom_height
  expr: Constraints[22] = <<param>>.terminal_offset
  expr: Constraints[23] = <<param>>.terminal_seperation
  sketch-geometry (17):
    g0: LineSegment StartX=10.25 StartY=-12.9 StartZ=0 EndX=11.25 EndY=-12.9 EndZ=0
    g1: LineSegment StartX=11.25 StartY=-12.9 StartZ=0 EndX=11.25 EndY=-19.5 EndZ=0
    g2: LineSegment StartX=11.25 StartY=-19.5 StartZ=0 EndX=10.25 EndY=-19.5 EndZ=0
    g3: LineSegment StartX=10.25 StartY=-19.5 StartZ=0 EndX=10.25 EndY=-17.25 EndZ=0
    g4: LineSegment StartX=-10.25 StartY=-12.9 StartZ=0 EndX=-11.25 EndY=-12.9 EndZ=0
    g5: LineSegment StartX=-11.25 StartY=-12.9 StartZ=0 EndX=-11.25 EndY=-19.5 EndZ=0
    g6: LineSegment StartX=-11.25 StartY=-19.5 StartZ=0 EndX=-10.25 EndY=-19.5 EndZ=0
    g7: LineSegment StartX=-10.25 StartY=-19.5 StartZ=0 EndX=-10.25 EndY=-17.25 EndZ=0
    g8: Circle [constr] CenterX=0 CenterY=-24 CenterZ=0 NormalX=0 NormalY=0 NormalZ=1 AngleXU=0 Radius=3
    g9: LineSegment StartX=-10.25 StartY=-15.15 StartZ=0 EndX=-8.75 EndY=-15.15 EndZ=0
    g10: LineSegment StartX=-10.25 StartY=-17.25 StartZ=0 EndX=-8.75 EndY=-17.25 EndZ=0
    g11: LineSegment StartX=-8.75 StartY=-15.15 StartZ=0 EndX=-8.75 EndY=-17.25 EndZ=0
    g12: LineSegment StartX=10.25 StartY=-15.15 StartZ=0 EndX=8.75 EndY=-15.15 EndZ=0
    g13: LineSegment StartX=8.75 StartY=-15.15 StartZ=0 EndX=8.75 EndY=-17.25 EndZ=0
    g14: LineSegment StartX=8.75 StartY=-17.25 StartZ=0 EndX=10.25 EndY=-17.25 EndZ=0
    g15: LineSegment StartX=-10.25 StartY=-15.15 StartZ=0 EndX=-10.25 EndY=-12.9 EndZ=0
    g16: LineSegment StartX=10.25 StartY=-15.15 StartZ=0 EndX=10.25 EndY=-12.9 EndZ=0
  constraints (48):
    c: Coincident(g0,g1)
    c: Coincident(g1,g2)
    c: Coincident(g2,g3)
    c: Coincident(g16,g0)
    c: Horizontal(g0)
    c: Horizontal(g2)
    c: Vertical(g1)
    c: Vertical(g3)
    c: Coincident(g4,g5)
    c: Coincident(g5,g6)
    c: Coincident(g6,g7)
    c: Coincident(g15,g4)
    c: Horizontal(g4)
    c: Horizontal(g6)
    c: Vertical(g5)
    c: Vertical(g7)
    c: Equal(g4,g0)
    c: DistanceX(g4,g4) = 1
    c: DistanceY(g3,g16) = 6.6
    c: PointOnObject(g8,g-2)
    c: Radius(g8) = 3
    c: DistanceY(g8,g-1) = 24
    c: DistanceY(g8,g1) = 4.5
    c: DistanceX(g6,g1) = 21.5
    c: Symmetric(g4,g0,g-2)
    c: Horizontal(g9)
    c: Horizontal(g10)
    c: Coincident(g11,g9)
    c: Coincident(g11,g10)
    c: Vertical(g11)
    c: Horizontal(g12)
    c: Coincident(g13,g12)
    c: Vertical(g13)
    c: Coincident(g14,g13)
    c: Horizontal(g14)
    c: Coincident(g7,g10)
    c: Coincident(g15,g9)
    c: Tangent(g7,g15)
    c: Coincident(g3,g14)
    c: Coincident(g16,g12)
    c: Tangent(g3,g16)
    c: Equal(g15,g7)
    c: Equal(g7,g3)
    c: Equal(g3,g16)
    c: Equal(g10,g14)
    c: Equal(g11,g13)
    c: DistanceY(g11,g11) = 2.1
    c: DistanceX(g12,g12) = 1.5
FEATURE [Sketcher::SketchObject] Sketch029  label="SketchAccess"
  ArcFitTolerance = 0
  AttachmentOffset = pos=(0,0,-20.5) rot=(0,0,1;0rad)
  AttachmentSupport = -> [XY_Plane005]
  FullyConstrained = true
  MapMode = 5
  Placement = pos=(0,0,-20.5) rot=(0,0,1;0rad)
  Support = -> [XY_Plane005]
  TreeRank = 0
  expr: AttachmentOffset.Base.z = -<<param>>.bottom_height + <<param>>.terminal_offset - 1
  expr: Constraints[20] = <<param>>.mid_depth / 2
  expr: Constraints[9] = <<param>>.terminal_seperation + <<param>>.terminal_thickness * 2
  sketch-geometry (12):
    g0: LineSegment StartX=-11.75 StartY=41 StartZ=0 EndX=-11.75 EndY=18.5 EndZ=0
    g1: LineSegment StartX=-7.95 StartY=41 StartZ=0 EndX=-7.95 EndY=21 EndZ=0
    g2: LineSegment StartX=7.95 StartY=41 StartZ=0 EndX=7.95 EndY=21 EndZ=0
    g3: LineSegment StartX=11.75 StartY=41 StartZ=0 EndX=11.75 EndY=18.5 EndZ=0
    g4: LineSegment StartX=-11.75 StartY=41 StartZ=0 EndX=-7.95 EndY=41 EndZ=0
    g5: LineSegment StartX=7.95 StartY=41 StartZ=0 EndX=11.75 EndY=41 EndZ=0
    g6: LineSegment StartX=-11.75 StartY=18.5 StartZ=0 EndX=-9.25 EndY=18.5 EndZ=0
    g7: LineSegment StartX=11.75 StartY=18.5 StartZ=0 EndX=9.25 EndY=18.5 EndZ=0
    g8: LineSegment StartX=-9.25 StartY=18.5 StartZ=0 EndX=-9.25 EndY=19.5 EndZ=0
    g9: LineSegment StartX=-9.25 StartY=19.5 StartZ=0 EndX=-7.95 EndY=21 EndZ=0
    g10: LineSegment StartX=9.25 StartY=18.5 StartZ=0 EndX=9.25 EndY=19.5 EndZ=0
    g11: LineSegment StartX=9.25 StartY=19.5 StartZ=0 EndX=7.95 EndY=21 EndZ=0
  constraints (35):
    c: Vertical(g0)
    c: Vertical(g2)
    c: Equal(g1,g2)
    c: Coincident(g4,g0)
    c: Coincident(g4,g1)
    c: Horizontal(g4)
    c: Coincident(g5,g2)
    c: Coincident(g5,g3)
    c: Horizontal(g5)
    c: DistanceX(g0,g3) = 23.5
    c: Vertical(g3)
    c: Equal(g5,g4)
    c: Symmetric(g1,g2,g-2)
    c: DistanceX(g4,g4) = 3.8
    c: Vertical(g1)
    c: Equal(g0,g3)
    c: Coincident(g6,g0)
    c: Horizontal(g6)
    c: Coincident(g7,g3)
    c: Equal(g6,g7)
    c: DistanceY(g-1,g3) = 41
    c: Horizontal(g7)
    c: Coincident(g8,g6)
    c: Vertical(g8)
    c: Coincident(g9,g8)
    c: Coincident(g9,g1)
    c: Coincident(g10,g7)
    c: Coincident(g11,g10)
    c: Coincident(g11,g2)
    c: Equal(g8,g10)
    c: Equal(g9,g11)
    c: DistanceY(g1,g1) = 20
    c: DistanceY(g0,g0) = 22.5
    c: DistanceX(g6,g6) = 2.5
    c: DistanceY(g8,g8) = 1
FEATURE [Sketcher::SketchObject] Sketch030  label="SketchFront"
  ArcFitTolerance = 0
  AttachmentOffset = pos=(0,0,41) rot=(0,0,1;0rad)
  AttachmentSupport = -> [XZ_Plane006]
  FullyConstrained = true
  MapMode = 5
  Placement = pos=(0,-41,-9.1e-15) rot=(1,0,0;1.5708rad)
  Support = -> [XZ_Plane006]
  TreeRank = 0
  expr: AttachmentOffset.Base.z = <<param>>.mid_depth / 2
  expr: Constraints[10] = <<param>>.front_width2
  expr: Constraints[11] = <<param>>.front_width2
  expr: Constraints[12] = <<param>>.front_height + 2
  expr: Constraints[24] = <<param>>.radius_big * 1.2
  expr: Constraints[25] = <<param>>.radius_big
  expr: Constraints[6] = <<param>>.radius_small
  expr: Constraints[7] = <<param>>.bottom_width
  expr: Constraints[9] = <<param>>.bottom_height
  sketch-geometry (12):
    g0: LineSegment StartX=-47 StartY=42 StartZ=0 EndX=47 EndY=42 EndZ=0
    g1: LineSegment StartX=47 StartY=42 StartZ=0 EndX=47 EndY=9.3923 EndZ=0
    g2: LineSegment StartX=36 StartY=-9.66025 StartZ=0 EndX=36 EndY=-21 EndZ=0
    g3: LineSegment StartX=33 StartY=-24 StartZ=0 EndX=-33 EndY=-24 EndZ=0
    g4: LineSegment StartX=-36 StartY=-21 StartZ=0 EndX=-36 EndY=-9.66025 EndZ=0
    g5: LineSegment StartX=-47 StartY=9.3923 StartZ=0 EndX=-47 EndY=42 EndZ=0
    g6: ArcOfCircle CenterX=-33 CenterY=-21 CenterZ=0 NormalX=0 NormalY=0 NormalZ=1 AngleXU=0 Radius=3 StartAngle=3.14159 EndAngle=4.71239
    g7: ArcOfCircle CenterX=33 CenterY=-21 CenterZ=0 NormalX=0 NormalY=0 NormalZ=1 AngleXU=0 Radius=3 StartAngle=4.71239 EndAngle=6.28319
    g8: ArcOfCircle CenterX=46 CenterY=-9.66025 CenterZ=0 NormalX=0 NormalY=0 NormalZ=1 AngleXU=0 Radius=10 StartAngle=2.0944 EndAngle=3.14159
    g9: ArcOfCircle CenterX=35 CenterY=9.3923 CenterZ=0 NormalX=0 NormalY=0 NormalZ=1 AngleXU=0 Radius=12 StartAngle=5.23599 EndAngle=6.28319
    g10: ArcOfCircle CenterX=-46 CenterY=-9.66025 CenterZ=0 NormalX=0 NormalY=0 NormalZ=1 AngleXU=0 Radius=10 StartAngle=0 EndAngle=1.0472
    g11: ArcOfCircle CenterX=-35 CenterY=9.3923 CenterZ=0 NormalX=0 NormalY=0 NormalZ=1 AngleXU=0 Radius=12 StartAngle=3.14159 EndAngle=4.18879
  constraints (30):
    c: Vertical(g2)
    c: Vertical(g4)
    c: Tangent(g4,g6) = 1.5708
    c: Tangent(g3,g6) = 1.5708
    c: Tangent(g3,g7) = 1.5708
    c: Tangent(g2,g7) = 1.5708
    c: Radius(g7) = 3
    c: DistanceX(g4,g2) = 72
    c: Symmetric(g3,g3,g-2)
    c: DistanceY(g3,g-1) = 24
    c: DistanceX(g5,g1) = 94
    c: DistanceX(g5,g1) = 94
    c: DistanceY(g3,g0) = 66
    c: Equal(g7,g6)
    c: Symmetric(g5,g1,g-2)
    c: Equal(g4,g2)
    c: Coincident(g0,g1)
    c: Coincident(g5,g0)
    c: Symmetric(g0,g0,g-2)
    c: Tangent(g10,g4) = -1.5708
    c: Tangent(g8,g2) = -1.5708
    c: Coincident(g11,g10)
    c: DistanceY(g8,g-1) = 1
    c: Equal(g9,g11)
    c: Radius(g9) = 12
    c: Radius(g8) = 10
    c: Equal(g8,g10)
    c: Tangent(g11,g5) = 1.5708
    c: Tangent(g1,g9) = 1.5708
    c: Tangent(g8,g9) = 1.5708
FEATURE [Sketcher::SketchObject] Sketch031  label="SketchRear"
  ArcFitTolerance = 0
  AttachmentOffset = pos=(0,0,-46) rot=(0,0,1;0rad)
  AttachmentSupport = -> [XZ_Plane006]
  FullyConstrained = true
  MapMode = 5
  Placement = pos=(0,46,1.02e-14) rot=(1,0,0;1.5708rad)
  Support = -> [XZ_Plane006]
  TreeRank = 0
  expr: AttachmentOffset.Base.z = -<<param>>.mid_depth / 2 - <<param>>.back_thickness
  expr: Constraints[15] = <<param>>.front_height + 2
  expr: Constraints[1] = <<param>>.radius_small
  expr: Constraints[2] = <<param>>.bottom_height
  expr: Constraints[3] = <<param>>.rear_width
  sketch-geometry (6):
    g0: LineSegment StartX=-33 StartY=-24 StartZ=0 EndX=33 EndY=-24 EndZ=0
    g1: LineSegment StartX=36 StartY=42 StartZ=0 EndX=-36 EndY=42 EndZ=0
    g2: ArcOfCircle CenterX=-33 CenterY=-21 CenterZ=0 NormalX=0 NormalY=0 NormalZ=1 AngleXU=0 Radius=3 StartAngle=3.14159 EndAngle=4.71239
    g3: ArcOfCircle CenterX=33 CenterY=-21 CenterZ=0 NormalX=0 NormalY=0 NormalZ=1 AngleXU=0 Radius=3 StartAngle=4.71239 EndAngle=6.28319
    g4: LineSegment StartX=36 StartY=-21 StartZ=0 EndX=36 EndY=42 EndZ=0
    g5: LineSegment StartX=-36 StartY=-21 StartZ=0 EndX=-36 EndY=42 EndZ=0
  constraints (19):
    c: Horizontal(g0)
    c: Radius(g3) = 3
    c: DistanceY(g0,g-1) = 24
    c: DistanceX(g2,g3) = 72
    c: Coincident(g4,g3)
    c: Vertical(g4)
    c: Coincident(g5,g2)
    c: Equal(g5,g4)
    c: Horizontal(g3,g3)
    c: Horizontal(g2,g2)
    c: Equal(g2,g3)
    c: Coincident(g0,g2)
    c: Coincident(g0,g3)
    c: Vertical(g2,g0)
    c: Vertical(g5)
    c: DistanceY(g0,g1) = 66
    c: Symmetric(g4,g5,g-2)
    c: Coincident(g4,g1)
    c: Coincident(g5,g1)
FEATURE [Part::Plane] Plane002  label="Plane"
  AttacherType = Attacher::AttachEngine3D
  AttachmentSupport = -> [XZ_Plane006]
  Length = 152
  Placement = pos=(-75,41,-75) rot=(1,0,0;1.5708rad)
  Support = -> [XZ_Plane006]
  TreeRank = 0
  Width = 150
  expr: Placement.Base.y = <<param>>.mid_depth / 2
FEATURE [Sketcher::SketchObject] Sketch032  label="SketchBack"
  ArcFitTolerance = 0
  AttachmentSupport = -> [XZ_Plane]
  FullyConstrained = true
  MapMode = 5
  Placement = pos=(0,0,0) rot=(1,0,0;1.5708rad)
  Support = -> [XZ_Plane]
  TreeRank = 0
  expr: Constraints[10] = <<param>>.rear_screw_width1
  expr: Constraints[11] = <<param>>.reart_screw_width2
  expr: Constraints[12] = <<param>>.rear_screw_height
  expr: Constraints[15] = <<param>>.rear_screw_offset
  expr: Constraints[1] = <<param>>.bottom_height
  expr: Constraints[2] = <<param>>.rear_width
  expr: Constraints[9] = <<param>>.screw_hole + 1
  sketch-geometry (6):
    g0: LineSegment [constr] StartX=36 StartY=-24 StartZ=0 EndX=-36 EndY=-24 EndZ=0
    g1: Circle CenterX=-29 CenterY=8.9 CenterZ=0 NormalX=0 NormalY=0 NormalZ=1 AngleXU=0 Radius=1.75
    g2: Circle CenterX=0 CenterY=8.9 CenterZ=0 NormalX=0 NormalY=0 NormalZ=1 AngleXU=0 Radius=1.75
    g3: Circle CenterX=29 CenterY=8.9 CenterZ=0 NormalX=0 NormalY=0 NormalZ=1 AngleXU=0 Radius=1.75
    g4: Circle CenterX=-27.5 CenterY=-16.6 CenterZ=0 NormalX=0 NormalY=0 NormalZ=1 AngleXU=0 Radius=1.75
    g5: Circle CenterX=27.5 CenterY=-16.6 CenterZ=0 NormalX=0 NormalY=0 NormalZ=1 AngleXU=0 Radius=1.75
  constraints (16):
    c: Symmetric(g0,g0,g-2)
    c: DistanceY(g0,g-1) = 24
    c: DistanceX(g0,g0) = 72
    c: Symmetric(g1,g3,g-2)
    c: Symmetric(g4,g5,g-2)
    c: Equal(g4,g1)
    c: Equal(g1,g2)
    c: Equal(g2,g3)
    c: Equal(g3,g5)
    c: Diameter(g1) = 3.5
    c: DistanceX(g1,g3) = 58
    c: DistanceX(g4,g5) = 55
    c: DistanceY(g5,g3) = 25.5
    c: Horizontal(g1,g2)
    c: PointOnObject(g2,g-2)
    c: DistanceY(g0,g5) = 7.4
FEATURE [Part::Loft] Loft
  Closed = false
  MaxDegree = 5
  Ruled = false
  Sections = -> [Sketch030,Sketch031]
  Solid = true
  TreeRank = 0
FEATURE [Part::Extrusion] Extrude
  Base = -> Sketch012
  Dir = (1,-1e-16,1e-16)
  DirMode = 2
  FaceMakerClass = Part::FaceMakerBullseye
  InnerTaperAngle = 0
  InnerTaperAngleRev = 0
  LengthFwd = 100
  LengthRev = 0
  Solid = true
  Symmetric = true
  TreeRank = 0
FEATURE [Part::MultiCommon] Common
  Shapes = -> [Extrude,Loft]
  TreeRank = 0
FEATURE [Part::FeaturePython] Slice  # WARN: FeaturePython — macro-defined, semantics opaque (R4)
  Base = -> Common
  Mode = 1
  Tolerance = 0
  Tools = -> [Plane002]
  TreeRank = 0
FEATURE [Part::FeaturePython] Slice_child0  label="Slice.0"  # WARN: FeaturePython — macro-defined, semantics opaque (R4)
  Base = -> Slice
  FilterType = 1
  Invert = false
  OverrideMaxVal = 0
  TreeRank = 0
  WindowFrom = 80
  WindowTo = 100
  items = 0
FEATURE [Part::FeaturePython] Slice_child1  label="Slice.1"  # WARN: FeaturePython — macro-defined, semantics opaque (R4)
  Base = -> Slice
  FilterType = 1
  Invert = false
  OverrideMaxVal = 0
  TreeRank = 0
  WindowFrom = 80
  WindowTo = 100
  items = 1
FEATURE [App::DocumentObjectGroup] GrExplode_Slice  label="Exploded Slice"
  ClaimAllChildren = true
  ExportMode = 1
  Group = -> [Slice_child0,Slice_child1]
  TreeRank = 0
  _GroupVersion = 1
FEATURE [App::DocumentObjectGroup] Group001  label="BaseShape"
  ClaimAllChildren = true
  ExportMode = 1
  Group = -> [Common,Sketch012,Sketch031,Sketch030,Plane002,GrExplode_Slice]
  TreeRank = 0
  _GroupVersion = 1
FEATURE [PartDesign::FeatureBase] BaseFeature
  BaseFeature = -> Slice_child1
  NewSolid = false
  Suppress = false
  TreeRank = 0
FEATURE [PartDesign::Pocket] Pocket  label="PocketHoles"
  BaseFeature = -> BaseFeature
  ClaimChildren = false
  Fit = 0
  FitJoin = 0
  InnerFit = 0
  InnerFitJoin = 0
  InnerTaperAngle = 0
  InnerTaperAngleRev = 0
  Length = 5
  Length2 = 100
  Midplane = true
  NewSolid = false
  Profile = -> Sketch032
  Suppress = false
  TreeRank = 0
  Type = 1
  _ProfileBasedVersion = 0
FEATURE [PartDesign::Fillet] Fillet  label="FilletBig"
  Base = -> Pocket [Edge30,Edge63]
  BaseFeature = -> Pocket
  NewSolid = false
  Radius = 10
  SupportTransform = false
  Suppress = false
  TreeRank = 0
  expr: Radius = <<param>>.radius_big
FEATURE [PartDesign::FeatureBase] BaseFeature001
  BaseFeature = -> Slice_child0
  NewSolid = false
  Suppress = false
  TreeRank = 0
FEATURE [PartDesign::Pocket] Pocket001  label="PocketBatt"
  BaseFeature = -> BaseFeature001
  ClaimChildren = false
  Fit = 0
  FitJoin = 0
  InnerFit = 0
  InnerFitJoin = 0
  InnerTaperAngle = 0
  InnerTaperAngleRev = 0
  Length = 14.6
  Length2 = 100
  NewSolid = false
  Profile = -> Sketch018
  Reversed = true
  Suppress = false
  TreeRank = 0
  Type = 0
  _ProfileBasedVersion = 0
  expr: Length = <<param>>.batt_carveout
FEATURE [PartDesign::Pad] Pad  label="PadBatt"
  BaseFeature = -> Pocket001
  ClaimChildren = false
  Direction = (1,1,1)
  Fit = 0
  FitJoin = 0
  InnerFit = 0
  InnerFitJoin = 0
  InnerTaperAngle = 0
  InnerTaperAngleRev = 0
  Length = 45
  Length2 = 100
  NewSolid = false
  Profile = -> Sketch019
  Suppress = false
  TreeRank = 0
  Type = 0
  _ProfileBasedVersion = 0
  expr: Length = <<param>>.batt_rail_length
FEATURE [PartDesign::Pocket] Pocket002  label="PocketSupport"
  BaseFeature = -> Pad
  ClaimChildren = false
  Fit = 0
  FitJoin = 0
  InnerFit = 0
  InnerFitJoin = 0
  InnerTaperAngle = 0
  InnerTaperAngleRev = 0
  Length = 5
  Length2 = 100
  NewSolid = false
  Profile = -> Sketch
  Suppress = false
  TreeRank = 0
  Type = 0
  _ProfileBasedVersion = 0
FEATURE [PartDesign::Pocket] Pocket006  label="PocketTerminal"
  BaseFeature = -> Pocket002
  ClaimChildren = false
  Fit = 0
  FitJoin = 0
  InnerFit = 0
  InnerFitJoin = 0
  InnerTaperAngle = 0
  InnerTaperAngleRev = 0
  Length = 18.5
  Length2 = 100
  NewSolid = false
  Profile = -> Sketch028
  Suppress = false
  TreeRank = 0
  Type = 0
  _ProfileBasedVersion = 0
  expr: Length = <<param>>.mid_depth / 2 - <<param>>.terminal_depth
FEATURE [PartDesign::Pocket] Pocket005  label="PocketAccess"
  BaseFeature = -> Pocket006
  ClaimChildren = false
  Fit = 0
  FitJoin = 0
  InnerFit = 0
  InnerFitJoin = 0
  InnerTaperAngle = 0
  InnerTaperAngleRev = 0
  Length = 22.5
  Length2 = 100
  NewSolid = false
  Profile = -> Sketch029
  Reversed = true
  Suppress = false
  TreeRank = 0
  Type = 0
  _ProfileBasedVersion = 0
  expr: Length = <<param>>.terminal_depth
FEATURE [Sketcher::SketchObject] Sketch033  label="SketchFace"
  ArcFitTolerance = 0
  AttachmentSupport = -> [XZ_Plane007]
  FullyConstrained = true
  MapMode = 5
  Placement = pos=(0,0,0) rot=(1,0,0;1.5708rad)
  Support = -> [XZ_Plane007]
  TreeRank = 0
  expr: Constraints[12] = <<param>>.face_radius
  expr: Constraints[21] = <<param>>.face_width1 - <<param>>.face_fit
  expr: Constraints[22] = <<param>>.face_width2 - 0.2
  expr: Constraints[23] = <<param>>.face_height - <<param>>.face_fit
  expr: Constraints[27] = <<param>>.screw_hole + 0.8
  expr: Constraints[28] = <<param>>.front_screw_width2 / 2
  expr: Constraints[29] = <<param>>.front_screw_width2 / 2
  expr: Constraints[30] = <<param>>.front_screw_width1 / 2
  expr: Constraints[31] = <<param>>.front_screw_width1 / 2
  expr: Constraints[32] = <<param>>.front_screw_height
  expr: Constraints[35] = <<param>>.front_screw_offset + <<param>>.face_offset - <<param>>.face_fit / 2
  expr: Constraints[48] = <<param>>.face_offset
  expr: Constraints[51] = <<param>>.face_knob_hole / 2
  expr: Constraints[52] = <<param>>.face_knob_x
  expr: Constraints[53] = <<param>>.face_offset + <<param>>.face_knob_y
  expr: Constraints[54] = <<param>>.face_screen_width - 2 * <<param>>.face_screen_radius
  expr: Constraints[55] = <<param>>.face_screen_height - 2 * <<param>>.face_screen_radius
  expr: Constraints[56] = <<param>>.face_offset + <<param>>.face_screen_y - <<param>>.face_screen_height / 2
  expr: Constraints[57] = <<param>>.face_screen_radius
  expr: Constraints[69] = <<param>>.face_plug_hole / 2
  expr: Constraints[71] = <<param>>.face_plug_y + <<param>>.face_offset
  expr: Constraints[72] = <<param>>.face_plug_x
  expr: Constraints[74] = <<param>>.face_screen_x
  sketch-geometry (25):
    g0: LineSegment StartX=-33.8084 StartY=37.4 StartZ=0 EndX=33.8084 EndY=37.4 EndZ=0
    g1: LineSegment StartX=41.8 StartY=29.7652 StartZ=0 EndX=42.65 EndY=11.1652 EndZ=0
    g2: LineSegment StartX=34.6584 StartY=2.8 StartZ=0 EndX=-34.6584 EndY=2.8 EndZ=0
    g3: LineSegment StartX=-42.65 StartY=11.1652 StartZ=0 EndX=-41.8 EndY=29.7652 EndZ=0
    g4: ArcOfCircle CenterX=33.8083 CenterY=29.4 CenterZ=0 NormalX=0 NormalY=0 NormalZ=1 AngleXU=0 Radius=8 StartAngle=0.0456652 EndAngle=1.57079
    g5: ArcOfCircle CenterX=34.6583 CenterY=10.8 CenterZ=0 NormalX=0 NormalY=0 NormalZ=1 AngleXU=0 Radius=8 StartAngle=4.71239 EndAngle=6.32885
    g6: ArcOfCircle CenterX=-33.8083 CenterY=29.4 CenterZ=0 NormalX=0 NormalY=0 NormalZ=1 AngleXU=0 Radius=8 StartAngle=1.5708 EndAngle=3.09593
    g7: ArcOfCircle CenterX=-34.6583 CenterY=10.8 CenterZ=0 NormalX=0 NormalY=0 NormalZ=1 AngleXU=0 Radius=8 StartAngle=3.09593 EndAngle=4.71239
    g8: Circle CenterX=-36.75 CenterY=32.1 CenterZ=0 NormalX=0 NormalY=0 NormalZ=1 AngleXU=0 Radius=1.65
    g9: Circle CenterX=36.75 CenterY=32.1 CenterZ=0 NormalX=0 NormalY=0 NormalZ=1 AngleXU=0 Radius=1.65
    g10: Circle CenterX=-38 CenterY=8.1 CenterZ=0 NormalX=0 NormalY=0 NormalZ=1 AngleXU=0 Radius=1.65
    g11: Circle CenterX=38 CenterY=8.1 CenterZ=0 NormalX=0 NormalY=0 NormalZ=1 AngleXU=0 Radius=1.65
    g12: LineSegment StartX=-11.25 StartY=30.35 StartZ=0 EndX=8.75 EndY=30.35 EndZ=0
    g13: LineSegment StartX=11 StartY=28.1 StartZ=0 EndX=11 EndY=19.5 EndZ=0
    g14: LineSegment StartX=8.75 StartY=17.25 StartZ=0 EndX=-11.25 EndY=17.25 EndZ=0
    g15: LineSegment StartX=-13.5 StartY=19.5 StartZ=0 EndX=-13.5 EndY=28.1 EndZ=0
    g16: ArcOfCircle CenterX=-11.25 CenterY=28.1 CenterZ=0 NormalX=0 NormalY=0 NormalZ=1 AngleXU=0 Radius=2.25 StartAngle=1.5708 EndAngle=3.14159
    g17: ArcOfCircle CenterX=-11.25 CenterY=19.5 CenterZ=0 NormalX=0 NormalY=0 NormalZ=1 AngleXU=0 Radius=2.25 StartAngle=3.14159 EndAngle=4.71239
    g18: ArcOfCircle CenterX=8.75 CenterY=19.5 CenterZ=0 NormalX=0 NormalY=0 NormalZ=1 AngleXU=0 Radius=2.25 StartAngle=4.71239 EndAngle=6.28319
    g19: ArcOfCircle CenterX=8.75 CenterY=28.1 CenterZ=0 NormalX=0 NormalY=0 NormalZ=1 AngleXU=0 Radius=2.25 StartAngle=-9e-16 EndAngle=1.5708
    g20: Circle CenterX=25.5 CenterY=23.3 CenterZ=0 NormalX=0 NormalY=0 NormalZ=1 AngleXU=0 Radius=3.7
    g21: LineSegment StartX=-30.35 StartY=25.9292 StartZ=0 EndX=-25.65 EndY=25.9292 EndZ=0
    g22: LineSegment StartX=-30.35 StartY=14.6708 StartZ=0 EndX=-25.65 EndY=14.6708 EndZ=0
    g23: ArcOfCircle CenterX=-28 CenterY=20.3 CenterZ=0 NormalX=0 NormalY=0 NormalZ=1 AngleXU=0 Radius=6.1 StartAngle=1.96627 EndAngle=4.31691
    g24: ArcOfCircle CenterX=-28 CenterY=20.3 CenterZ=0 NormalX=0 NormalY=0 NormalZ=1 AngleXU=0 Radius=6.1 StartAngle=5.10786 EndAngle=7.45851
  constraints (75):
    c: Coincident(g4,g0)
    c: Coincident(g4,g1)
    c: Coincident(g5,g1)
    c: Coincident(g5,g2)
    c: Coincident(g6,g0)
    c: Coincident(g6,g3)
    c: Coincident(g7,g3)
    c: Coincident(g7,g2)
    c: Equal(g1,g3)
    c: Equal(g4,g6)
    c: Equal(g6,g7)
    c: Equal(g7,g5)
    c: Radius(g4) = 8
    c: Tangent(g6,g3)
    c: Tangent(g7,g3)
    c: Tangent(g7,g2)
    c: Tangent(g6,g0)
    c: Tangent(g4,g0)
    c: Tangent(g4,g1)
    c: Tangent(g5,g1)
    c: Tangent(g5,g2)
    c: DistanceX(g3,g1) = 83.6
    c: DistanceX(g3,g1) = 85.3
    c: DistanceY(g2,g0) = 34.6
    c: Equal(g9,g8)
    c: Equal(g8,g10)
    c: Equal(g10,g11)
    c: Diameter(g8) = 3.3
    c: DistanceX(g10,g-1) = 38
    c: DistanceX(g-1,g11) = 38
    c: DistanceX(g-1,g9) = 36.75
    c: DistanceX(g8,g-1) = 36.75
    c: DistanceY(g11,g9) = 24
    c: Horizontal(g8,g9)
    c: Horizontal(g10,g11)
    c: DistanceY(g-1,g11) = 8.1
    c: Horizontal(g12)
    c: Horizontal(g14)
    c: Vertical(g13)
    c: Vertical(g15)
    c: Tangent(g15,g16) = 1.5708
    c: Tangent(g12,g16) = 1.5708
    c: Tangent(g15,g17) = 1.5708
    c: Tangent(g14,g17) = 1.5708
    c: Tangent(g14,g18) = 1.5708
    c: Tangent(g13,g18) = 1.5708
    c: Tangent(g12,g19) = 1.5708
    c: Tangent(g13,g19) = 1.5708
    c: DistanceY(g-1,g2) = 2.8
    c: Horizontal(g0)
    c: Symmetric(g2,g2,g-2)
    c: Radius(g20) = 3.7
    c: Distance(g20,g-2) = 25.5
    c: Distance(g20,g-1) = 23.3
    c: Distance(g12) = 20
    c: Distance(g15) = 8.6
    c: Distance(g14,g-1) = 17.25
    c: Radius(g19) = 2.25
    c: Equal(g19,g18)
    c: Equal(g18,g17)
    c: Equal(g17,g16)
    c: Horizontal(g21)
    c: Horizontal(g22)
    c: Equal(g21,g22)
    c: Coincident(g23,g21)
    c: Coincident(g23,g22)
    c: Coincident(g24,g23)
    c: Coincident(g24,g21)
    c: Coincident(g24,g22)
    c: Radius(g23) = 6.1
    c: Equal(g24,g23)
    c: Distance(g23,g-1) = 20.3
    c: Distance(g23,g-2) = 28
    c: Distance(g22) = 4.7
    c: Distance(g20,g13) = 14.5
FEATURE [PartDesign::Pad] Pad001  label="PadFace"
  ClaimChildren = false
  Direction = (1,1,1)
  Fit = 0
  FitJoin = 0
  InnerFit = 0
  InnerFitJoin = 0
  InnerTaperAngle = 0
  InnerTaperAngleRev = 0
  Length = 3
  Length2 = 100
  NewSolid = false
  Placement = pos=(0,0,0) rot=(1,0,0;1.5708rad)
  Profile = -> Sketch033
  Suppress = false
  TreeRank = 0
  Type = 0
  _ProfileBasedVersion = 0
  expr: Length = <<param>>.face_thickness
FEATURE [PartDesign::Chamfer] Chamfer001  label="ChamferScreen"
  Angle = 45
  Base = -> Pad001 [Edge34]
  BaseFeature = -> Pad001
  ChamferType = 0
  FlipDirection = false
  NewSolid = false
  Placement = pos=(0,0,0) rot=(1,0,0;1.5708rad)
  Size = 2
  Size2 = 1
  SupportTransform = false
  Suppress = false
  TreeRank = 0
FEATURE [PartDesign::Chamfer] Chamfer002  label="ChamferScrewsFront"
  Angle = 45
  Base = -> Chamfer001 [Edge62,Edge60,Edge61,Edge59]
  BaseFeature = -> Chamfer001
  ChamferType = 0
  FlipDirection = false
  NewSolid = false
  Placement = pos=(0,0,0) rot=(1,0,0;1.5708rad)
  Size = 1.4
  Size2 = 1
  SupportTransform = false
  Suppress = false
  TreeRank = 0
FEATURE [PartDesign::Fillet] Fillet009  label="FilletRear"
  Base = -> Fillet [Edge8]
  BaseFeature = -> Fillet
  NewSolid = false
  Radius = 2.93
  SupportTransform = false
  Suppress = false
  TreeRank = 0
FEATURE [PartDesign::Chamfer] Chamfer  label="ChamferScrewsRear"
  Angle = 45
  Base = -> Fillet009 [Edge43,Edge44,Edge45,Edge71,Edge73]
  BaseFeature = -> Fillet009
  ChamferType = 0
  FlipDirection = false
  NewSolid = false
  Size = 1.4
  Size2 = 1
  SupportTransform = false
  Suppress = false
  TreeRank = 0
FEATURE [PartDesign::Body] Body  label="BodyBack"
  AutoGroupSolids = false
  BaseFeature = -> Slice_child1
  ClaimAllChildren = false
  ExportMode = 0
  Group = -> [BaseFeature,Sketch032,Pocket,Fillet,Fillet009,Chamfer]
  Origin = -> Origin
  Tip = -> Chamfer
  TreeRank = 0
  _ExportChildren = -> [BaseFeature,Pocket,Fillet,Fillet009,Chamfer]
  _GroupVersion = 1
FEATURE [Sketcher::SketchObject] Sketch034  label="SketchKey"
  ArcFitTolerance = 0
  AttachmentOffset = pos=(0,0,-41) rot=(0,0,1;0rad)
  AttachmentSupport = -> [XZ_Plane005]
  FullyConstrained = true
  MapMode = 5
  Placement = pos=(0,41,9.1e-15) rot=(1,0,0;1.5708rad)
  Support = -> [XZ_Plane005]
  TreeRank = 0
  expr: AttachmentOffset.Base.z = -<<param>>.mid_depth / 2
  expr: Constraints[21] = <<param>>.rear_screw_offset
  expr: Constraints[22] = <<param>>.reart_screw_width2
  expr: Constraints[23] = <<param>>.screw_hole / 2
  expr: Constraints[2] = <<param>>.bottom_height
  sketch-geometry (9):
    g0: Circle [constr] CenterX=0 CenterY=-24 CenterZ=0 NormalX=0 NormalY=0 NormalZ=1 AngleXU=0 Radius=3
    g1: LineSegment StartX=4.5 StartY=-24 StartZ=0 EndX=11.5 EndY=-24 EndZ=0
    g2: LineSegment StartX=11.5 StartY=-24 StartZ=0 EndX=11.5 EndY=-22.8 EndZ=0
    g3: LineSegment StartX=4.5 StartY=-24 StartZ=0 EndX=4.5 EndY=-22.8 EndZ=0
    g4: LineSegment StartX=5.5 StartY=-21.8 StartZ=0 EndX=10.5 EndY=-21.8 EndZ=0
    g5: ArcOfCircle CenterX=10.5 CenterY=-22.8 CenterZ=0 NormalX=0 NormalY=0 NormalZ=1 AngleXU=0 Radius=1 StartAngle=1.1e-15 EndAngle=1.5708
    g6: ArcOfCircle CenterX=5.5 CenterY=-22.8 CenterZ=0 NormalX=0 NormalY=0 NormalZ=1 AngleXU=0 Radius=1 StartAngle=1.5708 EndAngle=3.14159
    g7: Circle CenterX=-27.5 CenterY=-16.6 CenterZ=0 NormalX=0 NormalY=0 NormalZ=1 AngleXU=0 Radius=1.25
    g8: Circle CenterX=27.5 CenterY=-16.6 CenterZ=0 NormalX=0 NormalY=0 NormalZ=1 AngleXU=0 Radius=1.25
  constraints (26):
    c: PointOnObject(g0,g-2)
    c: Radius(g0) = 3
    c: DistanceY(g0,g-1) = 24
    c: Horizontal(g1)
    c: Coincident(g2,g1)
    c: Vertical(g2)
    c: Coincident(g3,g1)
    c: Horizontal(g4)
    c: Coincident(g5,g2)
    c: Coincident(g6,g3)
    c: Equal(g5,g6)
    c: Equal(g3,g2)
    c: Tangent(g6,g4) = 1.5708
    c: Tangent(g5,g4) = 1.5708
    c: Vertical(g3)
    c: DistanceX(g1,g1) = 7
    c: DistanceY(g1,g4) = 2.2
    c: DistanceX(g-1,g1) = 4.5
    c: Radius(g6) = 1
    c: Horizontal(g0,g1)
    c: Horizontal(g3,g6)
    c: DistanceY(g0,g7) = 7.4
    c: DistanceX(g7,g8) = 55
    c: Radius(g7) = 1.25
    c: Equal(g7,g8)
    c: Symmetric(g7,g8,g-2)
FEATURE [PartDesign::Pocket] Pocket008  label="PocketKey"
  BaseFeature = -> Pocket005
  ClaimChildren = false
  Fit = 0
  FitJoin = 0
  InnerFit = 0
  InnerFitJoin = 0
  InnerTaperAngle = 0
  InnerTaperAngleRev = 0
  Length = 0
  Length2 = 100
  Midplane = true
  NewSolid = false
  Profile = -> Sketch034
  Suppress = false
  TreeRank = 0
  Type = 3
  UpToFace = -> Pocket005 [Face28]
  _ProfileBasedVersion = 0
FEATURE [PartDesign::SubtractiveLoft] SubtractiveLoft
  BaseFeature = -> Pocket008
  ClaimChildren = false
  Closed = false
  Fit = 0
  FitJoin = 0
  InnerFit = 0
  InnerFitJoin = 0
  NewSolid = false
  Profile = -> Sketch022
  Ruled = true
  Sections = -> [Sketch025,Sketch023]
  Suppress = false
  TreeRank = 0
  _ProfileBasedVersion = 0
FEATURE [PartDesign::Revolution] Revolution  label="RevolutionButton"
  Angle = 360
  Axis = (-3e-16,0.292372,0.956305)
  Base = (-3.1e-15,10,24)
  BaseFeature = -> SubtractiveLoft
  ClaimChildren = false
  Fit = 0
  FitJoin = 0
  InnerFit = 0
  InnerFitJoin = 0
  NewSolid = false
  Profile = -> Sketch021
  ReferenceAxis = -> Sketch021 [V_Axis]
  Reversed = true
  Suppress = false
  TreeRank = 0
  _ProfileBasedVersion = 0
FEATURE [PartDesign::Pocket] Pocket007  label="PocketButton"
  BaseFeature = -> Revolution
  ClaimChildren = false
  Fit = 0
  FitJoin = 0
  InnerFit = 0
  InnerFitJoin = 0
  InnerTaperAngle = 0
  InnerTaperAngleRev = 0
  Length = 14
  Length2 = 100
  NewSolid = false
  Profile = -> Sketch008
  Reversed = true
  Suppress = false
  TreeRank = 0
  Type = 0
  _ProfileBasedVersion = 0
FEATURE [PartDesign::Groove] Groove  label="GrooveButton"
  Angle = 360
  Axis = (-3e-16,0.292372,0.956305)
  Base = (-2.7e-15,10,22)
  BaseFeature = -> Pocket007
  ClaimChildren = false
  Fit = 0
  FitJoin = 0
  InnerFit = 0
  InnerFitJoin = 0
  NewSolid = false
  Profile = -> Sketch027
  ReferenceAxis = -> Sketch027 [V_Axis]
  Suppress = false
  TreeRank = 0
  _ProfileBasedVersion = 0
FEATURE [PartDesign::Pocket] Pocket004  label="PocketFrontScrews"
  BaseFeature = -> Groove
  ClaimChildren = false
  Fit = 0
  FitJoin = 0
  InnerFit = 0
  InnerFitJoin = 0
  InnerTaperAngle = 0
  InnerTaperAngleRev = 0
  Length = 5
  Length2 = 100
  NewSolid = false
  Profile = -> Sketch026
  Suppress = false
  TreeRank = 0
  Type = 0
  _ProfileBasedVersion = 0
FEATURE [PartDesign::Pocket] Pocket003  label="PocketFace"
  BaseFeature = -> Pocket004
  ClaimChildren = false
  Fit = 0
  FitJoin = 0
  InnerFit = 0
  InnerFitJoin = 0
  InnerTaperAngle = 0
  InnerTaperAngleRev = 0
  Length = 3.1
  Length2 = 100
  NewSolid = false
  Profile = -> Sketch024
  Reversed = true
  Suppress = false
  TreeRank = 0
  Type = 0
  _ProfileBasedVersion = 0
  expr: Length = <<param>>.face_thickness + 0.1
FEATURE [PartDesign::Fillet] Fillet010  label="FilletButton"
  Base = -> Pocket003 [Edge202]
  BaseFeature = -> Pocket003
  NewSolid = false
  Radius = 10
  SupportTransform = false
  Suppress = false
  TreeRank = 0
FEATURE [Mesh::Feature] Mesh001  label="BodyBack (Meshed)"
  TreeRank = 0
FEATURE [Mesh::Feature] T12Face
  Placement = pos=(0,-35,20.3) rot=(1,0,0;1.5708rad)
  TreeRank = 1
FEATURE [Sketcher::SketchObject] Sketch035  label="SketchTab"
  ArcFitTolerance = 1e-06
  AttachmentSupport = -> [XZ_Plane007]
  FullyConstrained = true
  MapMode = 5
  Placement = pos=(0,0,0) rot=(1,0,0;1.5708rad)
  Support = -> [XZ_Plane007]
  TreeRank = 8
  expr: Constraints[0] = <<param>>.face_offset + Spreadsheet.face_knob_y + <<param>>.face_knob_tab
  expr: Constraints[2] = <<param>>.face_knob_x
  sketch-geometry (1):
    g0: Circle CenterX=25.5 CenterY=30.3 CenterZ=0 NormalX=0 NormalY=0 NormalZ=1 AngleXU=0 Radius=1.5
  constraints (3):
    c: Distance(g0,g-1) = 30.3
    c: Radius(g0) = 1.5
    c: Distance(g0,g-2) = 25.5
FEATURE [PartDesign::Pocket] Pocket009  label="PocketTab"
  BaseFeature = -> Chamfer002
  ClaimChildren = false
  Fit = 0
  FitJoin = 0
  InnerFit = 0
  InnerFitJoin = 0
  InnerTaperAngle = 0
  InnerTaperAngleRev = 0
  Length = 1.5
  Length2 = 100
  Linearize = true
  NewSolid = false
  Placement = pos=(0,0,0) rot=(1,0,0;1.5708rad)
  Profile = -> Sketch035
  Reversed = true
  Suppress = false
  TreeRank = 9
  Type = 0
  _ProfileBasedVersion = 1
  expr: Length = <<param>>.face_thickness / 2
FEATURE [PartDesign::Body] Body005  label="BodyOLED"
  AutoGroupSolids = false
  ClaimAllChildren = false
  ExportMode = 0
  Group = -> [Sketch033,Pad001,Chamfer001,Chamfer002,Sketch035,Pocket009]
  Origin = -> Origin007
  Placement = pos=(0,-38,0) rot=(1,0,0;-0.349066rad)
  Tip = -> Pocket009
  TreeRank = 0
  _ExportChildren = -> [Pad001,Chamfer001,Chamfer002,Pocket009]
  _GroupVersion = 1
  expr: Placement.Base.y = -<<param>>.mid_depth / 2 + <<param>>.face_thickness
  expr: Placement.Rotation.Angle = -<<param>>.front_angle
FEATURE [Mesh::Feature] Mesh  label="BodyOLED (Meshed)"
  TreeRank = 12
FEATURE [PartDesign::Fillet] Fillet011  label="FilletBig1"
  Base = -> Fillet010 [Edge5]
  BaseFeature = -> Fillet010
  NewSolid = false
  Radius = 10
  SupportTransform = false
  Suppress = false
  TreeRank = 13
  expr: Radius = <<param>>.radius_big
FEATURE [PartDesign::Fillet] Fillet012  label="FilletBig2"
  Base = -> Fillet011 [Edge3]
  BaseFeature = -> Fillet011
  NewSolid = false
  Radius = 10
  SupportTransform = false
  Suppress = false
  TreeRank = 14
  expr: Radius = <<param>>.radius_big
FEATURE [PartDesign::Fillet] Fillet013  label="FilletFaceUpper"
  Base = -> Fillet012 [Edge10,Edge8,Edge1,Edge9,Edge11]
  BaseFeature = -> Fillet012
  NewSolid = false
  Radius = 2
  SupportTransform = false
  Suppress = false
  TreeRank = 15
FEATURE [PartDesign::Fillet] Fillet014  label="FilletFaceLower"
  Base = -> Fillet013 [Edge97,Edge100]
  BaseFeature = -> Fillet013
  NewSolid = false
  Radius = 2
  SupportTransform = false
  Suppress = false
  TreeRank = 16
FEATURE [PartDesign::Body] Body004  label="BodyCase"
  AutoGroupSolids = false
  BaseFeature = -> Slice_child0
  ClaimAllChildren = false
  ExportMode = 0
  Group = -> [BaseFeature001,Sketch008,Sketch029,Sketch018,Sketch019,Sketch021,Sketch022,Sketch023,Sketch024,Sketch025,Sketch026,Sketch027,Sketch028,Sketch,Pocket001,Pad,Pocket002,Pocket006,Pocket005,Pocket008,Sketch034,SubtractiveLoft,Revolution,Pocket007,Groove,Pocket004,Pocket003,Fillet010,Fillet011,Fillet012,Fillet013,Fillet014]
  Origin = -> Origin005
  Tip = -> Fillet014
  TreeRank = 0
  _ExportChildren = -> [BaseFeature001,Pocket001,Pad,Pocket002,Pocket006,Pocket005,Pocket008,SubtractiveLoft,Revolution,Pocket007,Groove,Pocket004,Pocket003,Fillet010,Fillet011,Fillet012,Fillet013,Fillet014]
  _GroupVersion = 1
FEATURE [Mesh::Feature] Mesh002  label="BodyCase (Meshed)"
  TreeRank = 17
FEATURE [App::DocumentObjectGroup] Group002  label="Mesh"
  ClaimAllChildren = true
  ExportMode = 1
  Group = -> [Mesh001,T12Face,Mesh,Mesh002]
  TreeRank = 0
  _GroupVersion = 1
FEATURE [App::Part] Part
  ClaimAllChildren = false
  ExportMode = 1
  Group = -> [Extrude,Plane002,Common,Sketch012,Loft,Slice_child1,Slice_child0,Slice,GrExplode_Slice,Sketch030,Sketch031,Group001,Spreadsheet,Body,Body004,Body005,Group002,Mesh001,T12Face,Mesh,Mesh002]
  Origin = -> Origin006
  TreeRank = 0
  _ExportChildren = -> [Group001,Spreadsheet,Body,Body004,Body005,Group002]
  _GroupVersion = 1
